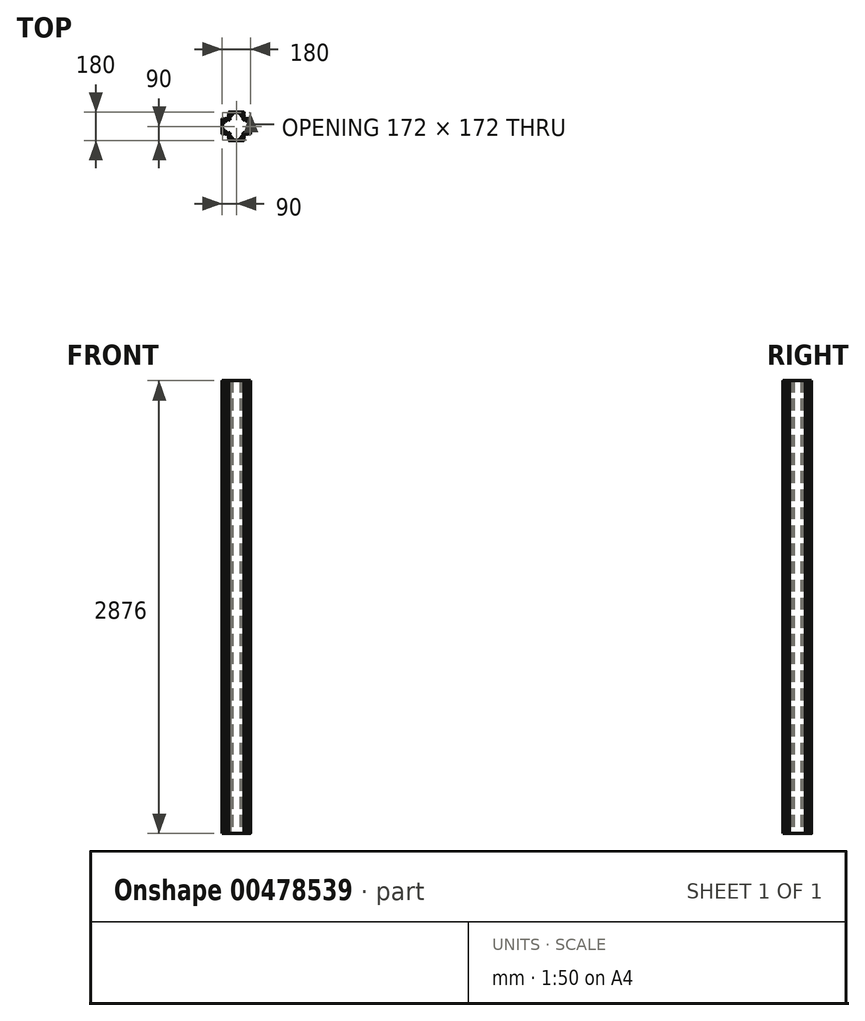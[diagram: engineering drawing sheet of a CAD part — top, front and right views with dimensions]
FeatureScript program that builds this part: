
annotation { "Feature Type Name" : "Feature", "Feature Type Description" : "" }
export const myFeature = defineFeature(function(context is Context, id is Id, definition is map)
    precondition{}
    {
        {
            var Q0;
            Q0=qCreatedBy(makeId("Top.planeOp"),FACE);
            var sketch = newSketch(context, id + "F0", { "sketchPlane" : qUnion([Q0])});
            skLineSegment(sketch, "E0", {"start": v(-58.4, 0) * mm, "end": v(68.52, 0) * mm, "construction": true});
            skLineSegment(sketch, "E1", {"start": v(0, 55.81) * mm, "end": v(0, -52.18) * mm, "construction": true});
            skLineSegment(sketch, "E2.bottom", {"start": v(-50, 90) * mm, "end": v(50, 90) * mm});
            skLineSegment(sketch, "E2.top", {"start": v(-50, -90) * mm, "end": v(50, -90) * mm});
            skLineSegment(sketch, "E2.left", {"start": v(-90, 50) * mm, "end": v(-90, -50) * mm});
            skLineSegment(sketch, "E2.right", {"start": v(90, 50) * mm, "end": v(90, -50) * mm});
            skLineSegment(sketch, "E3", {"start": v(-90, 50) * mm, "end": v(-82, 50) * mm});
            skLineSegment(sketch, "E4", {"start": v(-50, 50) * mm, "end": v(-50, 72) * mm});
            skLineSegment(sketch, "E5.MirrorCS", {"start": v(90, 50) * mm, "end": v(82, 50) * mm});
            skLineSegment(sketch, "E6.MirrorCS", {"start": v(50, 50) * mm, "end": v(50, 72) * mm});
            skLineSegment(sketch, "E7.MirrorCS", {"start": v(50, -50) * mm, "end": v(50, -72) * mm});
            skLineSegment(sketch, "E8.MirrorCS", {"start": v(90, -50) * mm, "end": v(82, -50) * mm});
            skLineSegment(sketch, "E9.MirrorCS", {"start": v(-50, -50) * mm, "end": v(-50, -72) * mm});
            skLineSegment(sketch, "E10.MirrorCS", {"start": v(-90, -50) * mm, "end": v(-82, -50) * mm});
            skLineSegment(sketch, "E11", {"start": v(-82, -50) * mm, "end": v(-82, -46) * mm});
            skLineSegment(sketch, "E12", {"start": v(-82, -46) * mm, "end": v(-86, -46) * mm});
            skLineSegment(sketch, "E13", {"start": v(-86, -46) * mm, "end": v(-86, -38) * mm});
            skLineSegment(sketch, "E14", {"start": v(-86, -38) * mm, "end": v(-68, -38) * mm});
            skLineSegment(sketch, "E15", {"start": v(-68, -38) * mm, "end": v(-68, -46) * mm});
            skLineSegment(sketch, "E16", {"start": v(-68, -46) * mm, "end": v(-72, -46) * mm});
            skLineSegment(sketch, "E17", {"start": v(-72, -46) * mm, "end": v(-72, -50) * mm});
            skLineSegment(sketch, "E18.MirrorCS", {"start": v(-68, 46) * mm, "end": v(-72, 46) * mm});
            skLineSegment(sketch, "E19.MirrorCS", {"start": v(-86, 38) * mm, "end": v(-68, 38) * mm});
            skLineSegment(sketch, "E20.MirrorCS", {"start": v(-82, 50) * mm, "end": v(-82, 46) * mm});
            skLineSegment(sketch, "E21.MirrorCS", {"start": v(-86, 46) * mm, "end": v(-86, 38) * mm});
            skLineSegment(sketch, "E22.MirrorCS", {"start": v(-82, 46) * mm, "end": v(-86, 46) * mm});
            skLineSegment(sketch, "E23.MirrorCS", {"start": v(-68, 38) * mm, "end": v(-68, 46) * mm});
            skLineSegment(sketch, "E24.MirrorCS", {"start": v(-72, 46) * mm, "end": v(-72, 50) * mm});
            skLineSegment(sketch, "E25.MirrorCS", {"start": v(68, -38) * mm, "end": v(68, -46) * mm});
            skLineSegment(sketch, "E26.MirrorCS", {"start": v(86, 38) * mm, "end": v(68, 38) * mm});
            skLineSegment(sketch, "E27.MirrorCS", {"start": v(82, 46) * mm, "end": v(86, 46) * mm});
            skLineSegment(sketch, "E28.MirrorCS", {"start": v(86, -38) * mm, "end": v(68, -38) * mm});
            skLineSegment(sketch, "E29.MirrorCS", {"start": v(68, 46) * mm, "end": v(72, 46) * mm});
            skLineSegment(sketch, "E30.MirrorCS", {"start": v(86, 46) * mm, "end": v(86, 38) * mm});
            skLineSegment(sketch, "E31.MirrorCS", {"start": v(86, -46) * mm, "end": v(86, -38) * mm});
            skLineSegment(sketch, "E32.MirrorCS", {"start": v(72, -46) * mm, "end": v(72, -50) * mm});
            skLineSegment(sketch, "E33.MirrorCS", {"start": v(82, 50) * mm, "end": v(82, 46) * mm});
            skLineSegment(sketch, "E34.MirrorCS", {"start": v(72, 46) * mm, "end": v(72, 50) * mm});
            skLineSegment(sketch, "E35.MirrorCS", {"start": v(68, 38) * mm, "end": v(68, 46) * mm});
            skLineSegment(sketch, "E36.MirrorCS", {"start": v(82, -50) * mm, "end": v(82, -46) * mm});
            skLineSegment(sketch, "E37.MirrorCS", {"start": v(68, -46) * mm, "end": v(72, -46) * mm});
            skLineSegment(sketch, "E38.MirrorCS", {"start": v(82, -46) * mm, "end": v(86, -46) * mm});
            skLineSegment(sketch, "E39", {"start": v(-50, 50) * mm, "end": v(0, 0) * mm, "construction": true});
            skLineSegment(sketch, "E40.MirrorCS", {"start": v(-38, 68) * mm, "end": v(-46, 68) * mm});
            skLineSegment(sketch, "E41.MirrorCS", {"start": v(-46, 68) * mm, "end": v(-46, 72) * mm});
            skLineSegment(sketch, "E42.MirrorCS", {"start": v(-46, 72) * mm, "end": v(-50, 72) * mm});
            skLineSegment(sketch, "E43.MirrorCS", {"start": v(-38, 86) * mm, "end": v(-38, 68) * mm});
            skLineSegment(sketch, "E44.MirrorCS", {"start": v(-46, 86) * mm, "end": v(-38, 86) * mm});
            skLineSegment(sketch, "E45.MirrorCS", {"start": v(-50, 82) * mm, "end": v(-46, 82) * mm});
            skLineSegment(sketch, "E46.MirrorCS", {"start": v(-46, 82) * mm, "end": v(-46, 86) * mm});
            skLineSegment(sketch, "E47.MirrorCS", {"start": v(46, 82) * mm, "end": v(46, 86) * mm});
            skLineSegment(sketch, "E48.MirrorCS", {"start": v(38, 86) * mm, "end": v(38, 68) * mm});
            skLineSegment(sketch, "E49.MirrorCS", {"start": v(46, 68) * mm, "end": v(46, 72) * mm});
            skLineSegment(sketch, "E50.MirrorCS", {"start": v(50, 82) * mm, "end": v(46, 82) * mm});
            skLineSegment(sketch, "E51.MirrorCS", {"start": v(46, 86) * mm, "end": v(38, 86) * mm});
            skLineSegment(sketch, "E52.MirrorCS", {"start": v(38, 68) * mm, "end": v(46, 68) * mm});
            skLineSegment(sketch, "E53.MirrorCS", {"start": v(46, 72) * mm, "end": v(50, 72) * mm});
            skLineSegment(sketch, "E54.MirrorCS", {"start": v(-46, -86) * mm, "end": v(-38, -86) * mm});
            skLineSegment(sketch, "E55.MirrorCS", {"start": v(50, -82) * mm, "end": v(46, -82) * mm});
            skLineSegment(sketch, "E56.MirrorCS", {"start": v(-38, -86) * mm, "end": v(-38, -68) * mm});
            skLineSegment(sketch, "E57.MirrorCS", {"start": v(-46, -82) * mm, "end": v(-46, -86) * mm});
            skLineSegment(sketch, "E58.MirrorCS", {"start": v(-38, -68) * mm, "end": v(-46, -68) * mm});
            skLineSegment(sketch, "E59.MirrorCS", {"start": v(38, -86) * mm, "end": v(38, -68) * mm});
            skLineSegment(sketch, "E60.MirrorCS", {"start": v(-50, -82) * mm, "end": v(-46, -82) * mm});
            skLineSegment(sketch, "E61.MirrorCS", {"start": v(-46, -72) * mm, "end": v(-50, -72) * mm});
            skLineSegment(sketch, "E62.MirrorCS", {"start": v(-46, -68) * mm, "end": v(-46, -72) * mm});
            skLineSegment(sketch, "E63.MirrorCS", {"start": v(46, -72) * mm, "end": v(50, -72) * mm});
            skLineSegment(sketch, "E64.MirrorCS", {"start": v(38, -68) * mm, "end": v(46, -68) * mm});
            skLineSegment(sketch, "E65.MirrorCS", {"start": v(46, -68) * mm, "end": v(46, -72) * mm});
            skLineSegment(sketch, "E66.MirrorCS", {"start": v(46, -82) * mm, "end": v(46, -86) * mm});
            skLineSegment(sketch, "E67.MirrorCS", {"start": v(46, -86) * mm, "end": v(38, -86) * mm});
            skLineSegment(sketch, "E68.trimOffspring", {"start": v(-72, 50) * mm, "end": v(-50, 50) * mm});
            skLineSegment(sketch, "E69.trimOffspring", {"start": v(-50, 82) * mm, "end": v(-50, 90) * mm});
            skLineSegment(sketch, "E70.trimOffspring", {"start": v(50, 82) * mm, "end": v(50, 90) * mm});
            skLineSegment(sketch, "E71.trimOffspring", {"start": v(72, 50) * mm, "end": v(50, 50) * mm});
            skLineSegment(sketch, "E72.trimOffspring", {"start": v(72, -50) * mm, "end": v(50, -50) * mm});
            skLineSegment(sketch, "E73.trimOffspring", {"start": v(50, -82) * mm, "end": v(50, -90) * mm});
            skLineSegment(sketch, "E74.trimOffspring", {"start": v(-50, -82) * mm, "end": v(-50, -90) * mm});
            skLineSegment(sketch, "E75.trimOffspring", {"start": v(-72, -50) * mm, "end": v(-50, -50) * mm});
            skSolve(sketch);
        }
        {
            var Q0;
            Q0 = qSketchRegion(id + "F0", true);
            extrude(context, id + "F1", {"entities" : qUnion([Q0]), "depth" : 2876 * mm, "offsetDistance" : 25 * mm});
        }
        {
            var Q0;
            Q0=makeQuery(id+"F1.opExtrude","CAP_FACE",FACE,{"disambiguationData":[OSD([sQuery(id+"F0.wireOp",EDGE,"E2.bottom"),sQuery(id+"F0.wireOp",EDGE,"E2.top"),sQuery(id+"F0.wireOp",EDGE,"E2.left"),sQuery(id+"F0.wireOp",EDGE,"E2.right"),sQuery(id+"F0.wireOp",EDGE,"E3"),sQuery(id+"F0.wireOp",EDGE,"E4"),sQuery(id+"F0.wireOp",EDGE,"E5.MirrorCS"),sQuery(id+"F0.wireOp",EDGE,"E6.MirrorCS"),sQuery(id+"F0.wireOp",EDGE,"E7.MirrorCS"),sQuery(id+"F0.wireOp",EDGE,"E8.MirrorCS"),sQuery(id+"F0.wireOp",EDGE,"E9.MirrorCS"),sQuery(id+"F0.wireOp",EDGE,"E10.MirrorCS")])],"isStart":false});
            var Q1;
            Q1=makeQuery(id+"F1.opExtrude","CAP_FACE",FACE,{"disambiguationData":[OSD([sQuery(id+"F0.wireOp",EDGE,"E2.bottom"),sQuery(id+"F0.wireOp",EDGE,"E2.top"),sQuery(id+"F0.wireOp",EDGE,"E2.left"),sQuery(id+"F0.wireOp",EDGE,"E2.right"),sQuery(id+"F0.wireOp",EDGE,"E3"),sQuery(id+"F0.wireOp",EDGE,"E4"),sQuery(id+"F0.wireOp",EDGE,"E5.MirrorCS"),sQuery(id+"F0.wireOp",EDGE,"E6.MirrorCS"),sQuery(id+"F0.wireOp",EDGE,"E7.MirrorCS"),sQuery(id+"F0.wireOp",EDGE,"E8.MirrorCS"),sQuery(id+"F0.wireOp",EDGE,"E9.MirrorCS"),sQuery(id+"F0.wireOp",EDGE,"E10.MirrorCS")])],"isStart":true});
            shell(context, id + "F2", {"entities" : qUnion([Q0, Q1]), "thickness" : 4 * mm});
        }
        {
            var Q0;
            Q0=makeQuery(id+"F1.opExtrude","SWEPT_EDGE",EDGE,{"disambiguationData":[OSD([sQuery(id+"F0.wireOp",EDGE,"E2.top"),sQuery(id+"F0.wireOp",EDGE,"E74.trimOffspring")])]});
            var Q1;
            Q1=makeQuery(id+"F1.opExtrude","SWEPT_EDGE",EDGE,{"disambiguationData":[OSD([sQuery(id+"F0.wireOp",EDGE,"E2.left"),sQuery(id+"F0.wireOp",EDGE,"E10.MirrorCS")])]});
            var Q2;
            Q2=makeQuery(id+"F1.opExtrude","SWEPT_EDGE",EDGE,{"disambiguationData":[OSD([sQuery(id+"F0.wireOp",EDGE,"E2.top"),sQuery(id+"F0.wireOp",EDGE,"E73.trimOffspring")])]});
            var Q3;
            Q3=makeQuery(id+"F1.opExtrude","SWEPT_EDGE",EDGE,{"disambiguationData":[OSD([sQuery(id+"F0.wireOp",EDGE,"E2.right"),sQuery(id+"F0.wireOp",EDGE,"E8.MirrorCS")])]});
            var Q4;
            Q4=makeQuery(id+"F1.opExtrude","SWEPT_EDGE",EDGE,{"disambiguationData":[OSD([sQuery(id+"F0.wireOp",EDGE,"E2.right"),sQuery(id+"F0.wireOp",EDGE,"E5.MirrorCS")])]});
            var Q5;
            Q5=makeQuery(id+"F1.opExtrude","SWEPT_EDGE",EDGE,{"disambiguationData":[OSD([sQuery(id+"F0.wireOp",EDGE,"E2.bottom"),sQuery(id+"F0.wireOp",EDGE,"E70.trimOffspring")])]});
            var Q6;
            Q6=makeQuery(id+"F1.opExtrude","SWEPT_EDGE",EDGE,{"disambiguationData":[OSD([sQuery(id+"F0.wireOp",EDGE,"E2.bottom"),sQuery(id+"F0.wireOp",EDGE,"E69.trimOffspring")])]});
            var Q7;
            Q7=makeQuery(id+"F1.opExtrude","SWEPT_EDGE",EDGE,{"disambiguationData":[OSD([sQuery(id+"F0.wireOp",EDGE,"E2.left"),sQuery(id+"F0.wireOp",EDGE,"E3")])]});
            fillet(context, id + "F3", {"entities" : qUnion([Q0, Q1, Q2, Q3, Q4, Q5, Q6, Q7]), "radius" : 3 * mm, "tangentPropagation" : true, "allowEdgeOverflow" : false});
        }
        {
            var Q0;
            Q0=makeQuery(id+"F1.opExtrude","CAP_FACE",FACE,{"disambiguationData":[OSD([sQuery(id+"F0.wireOp",EDGE,"E2.bottom"),sQuery(id+"F0.wireOp",EDGE,"E2.top"),sQuery(id+"F0.wireOp",EDGE,"E2.left"),sQuery(id+"F0.wireOp",EDGE,"E2.right"),sQuery(id+"F0.wireOp",EDGE,"E3"),sQuery(id+"F0.wireOp",EDGE,"E4"),sQuery(id+"F0.wireOp",EDGE,"E5.MirrorCS"),sQuery(id+"F0.wireOp",EDGE,"E6.MirrorCS"),sQuery(id+"F0.wireOp",EDGE,"E7.MirrorCS"),sQuery(id+"F0.wireOp",EDGE,"E8.MirrorCS"),sQuery(id+"F0.wireOp",EDGE,"E9.MirrorCS"),sQuery(id+"F0.wireOp",EDGE,"E10.MirrorCS"),sQuery(id+"F0.wireOp",EDGE,"E11"),sQuery(id+"F0.wireOp",EDGE,"E12"),sQuery(id+"F0.wireOp",EDGE,"E13"),sQuery(id+"F0.wireOp",EDGE,"E14"),sQuery(id+"F0.wireOp",EDGE,"E15"),sQuery(id+"F0.wireOp",EDGE,"E16"),sQuery(id+"F0.wireOp",EDGE,"E17"),sQuery(id+"F0.wireOp",EDGE,"E18.MirrorCS"),sQuery(id+"F0.wireOp",EDGE,"E19.MirrorCS"),sQuery(id+"F0.wireOp",EDGE,"E20.MirrorCS"),sQuery(id+"F0.wireOp",EDGE,"E21.MirrorCS"),sQuery(id+"F0.wireOp",EDGE,"E22.MirrorCS"),sQuery(id+"F0.wireOp",EDGE,"E23.MirrorCS"),sQuery(id+"F0.wireOp",EDGE,"E24.MirrorCS"),sQuery(id+"F0.wireOp",EDGE,"E25.MirrorCS"),sQuery(id+"F0.wireOp",EDGE,"E26.MirrorCS"),sQuery(id+"F0.wireOp",EDGE,"E27.MirrorCS"),sQuery(id+"F0.wireOp",EDGE,"E28.MirrorCS"),sQuery(id+"F0.wireOp",EDGE,"E29.MirrorCS"),sQuery(id+"F0.wireOp",EDGE,"E30.MirrorCS"),sQuery(id+"F0.wireOp",EDGE,"E31.MirrorCS"),sQuery(id+"F0.wireOp",EDGE,"E32.MirrorCS"),sQuery(id+"F0.wireOp",EDGE,"E33.MirrorCS"),sQuery(id+"F0.wireOp",EDGE,"E34.MirrorCS"),sQuery(id+"F0.wireOp",EDGE,"E35.MirrorCS"),sQuery(id+"F0.wireOp",EDGE,"E36.MirrorCS"),sQuery(id+"F0.wireOp",EDGE,"E37.MirrorCS"),sQuery(id+"F0.wireOp",EDGE,"E38.MirrorCS"),sQuery(id+"F0.wireOp",EDGE,"E40.MirrorCS"),sQuery(id+"F0.wireOp",EDGE,"E41.MirrorCS"),sQuery(id+"F0.wireOp",EDGE,"E42.MirrorCS"),sQuery(id+"F0.wireOp",EDGE,"E43.MirrorCS"),sQuery(id+"F0.wireOp",EDGE,"E44.MirrorCS"),sQuery(id+"F0.wireOp",EDGE,"E45.MirrorCS"),sQuery(id+"F0.wireOp",EDGE,"E46.MirrorCS"),sQuery(id+"F0.wireOp",EDGE,"E47.MirrorCS"),sQuery(id+"F0.wireOp",EDGE,"E48.MirrorCS"),sQuery(id+"F0.wireOp",EDGE,"E49.MirrorCS"),sQuery(id+"F0.wireOp",EDGE,"E50.MirrorCS"),sQuery(id+"F0.wireOp",EDGE,"E51.MirrorCS"),sQuery(id+"F0.wireOp",EDGE,"E52.MirrorCS"),sQuery(id+"F0.wireOp",EDGE,"E53.MirrorCS"),sQuery(id+"F0.wireOp",EDGE,"E54.MirrorCS"),sQuery(id+"F0.wireOp",EDGE,"E55.MirrorCS"),sQuery(id+"F0.wireOp",EDGE,"E56.MirrorCS"),sQuery(id+"F0.wireOp",EDGE,"E57.MirrorCS"),sQuery(id+"F0.wireOp",EDGE,"E58.MirrorCS"),sQuery(id+"F0.wireOp",EDGE,"E59.MirrorCS"),sQuery(id+"F0.wireOp",EDGE,"E60.MirrorCS"),sQuery(id+"F0.wireOp",EDGE,"E61.MirrorCS"),sQuery(id+"F0.wireOp",EDGE,"E62.MirrorCS"),sQuery(id+"F0.wireOp",EDGE,"E63.MirrorCS"),sQuery(id+"F0.wireOp",EDGE,"E64.MirrorCS"),sQuery(id+"F0.wireOp",EDGE,"E65.MirrorCS"),sQuery(id+"F0.wireOp",EDGE,"E66.MirrorCS"),sQuery(id+"F0.wireOp",EDGE,"E67.MirrorCS"),sQuery(id+"F0.wireOp",EDGE,"E68.trimOffspring"),sQuery(id+"F0.wireOp",EDGE,"E69.trimOffspring"),sQuery(id+"F0.wireOp",EDGE,"E70.trimOffspring"),sQuery(id+"F0.wireOp",EDGE,"E71.trimOffspring"),sQuery(id+"F0.wireOp",EDGE,"E72.trimOffspring"),sQuery(id+"F0.wireOp",EDGE,"E73.trimOffspring"),sQuery(id+"F0.wireOp",EDGE,"E74.trimOffspring"),sQuery(id+"F0.wireOp",EDGE,"E75.trimOffspring")])],"isStart":true});
            var sketch = newSketch(context, id + "F4", { "sketchPlane" : qUnion([Q0])});
            skLineSegment(sketch, "E76.bottom", {"start": v(-64, 38) * mm, "end": v(-61, 38) * mm});
            skLineSegment(sketch, "E76.top", {"start": v(-64, 34) * mm, "end": v(-61, 34) * mm});
            skLineSegment(sketch, "E76.left", {"start": v(-64, 38) * mm, "end": v(-64, 34) * mm});
            skLineSegment(sketch, "E76.right", {"start": v(-61, 38) * mm, "end": v(-61, 34) * mm});
            skLineSegment(sketch, "E77", {"start": v(-74, 34) * mm, "end": v(-74, 23) * mm});
            skLineSegment(sketch, "E78", {"start": v(-74, 23) * mm, "end": v(-78, 23) * mm});
            skLineSegment(sketch, "E79", {"start": v(-78, 23) * mm, "end": v(-78, 34) * mm});
            skLineSegment(sketch, "E80", {"start": v(-78, 34) * mm, "end": v(-74, 34) * mm});
            skLineSegment(sketch, "E81", {"start": v(0, 86) * mm, "end": v(0, 0) * mm, "construction": true});
            skLineSegment(sketch, "E82", {"start": v(0, 0) * mm, "end": v(-86, 0) * mm, "construction": true});
            skLineSegment(sketch, "E83.MirrorCS", {"start": v(64, 38) * mm, "end": v(64, 34) * mm});
            skLineSegment(sketch, "E84.MirrorCS", {"start": v(61, 38) * mm, "end": v(61, 34) * mm});
            skLineSegment(sketch, "E85.MirrorCS", {"start": v(78, 34) * mm, "end": v(74, 34) * mm});
            skLineSegment(sketch, "E86.MirrorCS", {"start": v(74, 23) * mm, "end": v(78, 23) * mm});
            skLineSegment(sketch, "E87.MirrorCS", {"start": v(64, 38) * mm, "end": v(61, 38) * mm});
            skLineSegment(sketch, "E88.MirrorCS", {"start": v(64, 34) * mm, "end": v(61, 34) * mm});
            skLineSegment(sketch, "E89.MirrorCS", {"start": v(78, 23) * mm, "end": v(78, 34) * mm});
            skLineSegment(sketch, "E90.MirrorCS", {"start": v(74, 34) * mm, "end": v(74, 23) * mm});
            skLineSegment(sketch, "E91.MirrorCS", {"start": v(0, 0) * mm, "end": v(86, 0) * mm, "construction": true});
            skLineSegment(sketch, "E92.MirrorCS", {"start": v(74, -34) * mm, "end": v(74, -23) * mm});
            skLineSegment(sketch, "E93.MirrorCS", {"start": v(74, -23) * mm, "end": v(78, -23) * mm});
            skLineSegment(sketch, "E94.MirrorCS", {"start": v(64, -38) * mm, "end": v(61, -38) * mm});
            skLineSegment(sketch, "E95.MirrorCS", {"start": v(64, -34) * mm, "end": v(61, -34) * mm});
            skLineSegment(sketch, "E96.MirrorCS", {"start": v(-64, -38) * mm, "end": v(-61, -38) * mm});
            skLineSegment(sketch, "E97.MirrorCS", {"start": v(-64, -34) * mm, "end": v(-61, -34) * mm});
            skLineSegment(sketch, "E98.MirrorCS", {"start": v(-64, -38) * mm, "end": v(-64, -34) * mm});
            skLineSegment(sketch, "E99.MirrorCS", {"start": v(-61, -38) * mm, "end": v(-61, -34) * mm});
            skLineSegment(sketch, "E100.MirrorCS", {"start": v(-74, -34) * mm, "end": v(-74, -23) * mm});
            skLineSegment(sketch, "E101.MirrorCS", {"start": v(-74, -23) * mm, "end": v(-78, -23) * mm});
            skLineSegment(sketch, "E102.MirrorCS", {"start": v(78, -34) * mm, "end": v(74, -34) * mm});
            skLineSegment(sketch, "E103.MirrorCS", {"start": v(61, -38) * mm, "end": v(61, -34) * mm});
            skLineSegment(sketch, "E104.MirrorCS", {"start": v(78, -23) * mm, "end": v(78, -34) * mm});
            skLineSegment(sketch, "E105.MirrorCS", {"start": v(-78, -34) * mm, "end": v(-74, -34) * mm});
            skLineSegment(sketch, "E106.MirrorCS", {"start": v(-78, -23) * mm, "end": v(-78, -34) * mm});
            skLineSegment(sketch, "E107.MirrorCS", {"start": v(64, -38) * mm, "end": v(64, -34) * mm});
            skLineSegment(sketch, "E108", {"start": v(-46, 46) * mm, "end": v(0, 0) * mm, "construction": true});
            skLineSegment(sketch, "E109.MirrorCS", {"start": v(-34, 78) * mm, "end": v(-34, 74) * mm});
            skLineSegment(sketch, "E110.MirrorCS", {"start": v(-23, 78) * mm, "end": v(-34, 78) * mm});
            skLineSegment(sketch, "E111.MirrorCS", {"start": v(-23, 74) * mm, "end": v(-23, 78) * mm});
            skLineSegment(sketch, "E112.MirrorCS", {"start": v(-34, 74) * mm, "end": v(-23, 74) * mm});
            skLineSegment(sketch, "E113.MirrorCS", {"start": v(-38, 61) * mm, "end": v(-34, 61) * mm});
            skLineSegment(sketch, "E114.MirrorCS", {"start": v(-38, 64) * mm, "end": v(-34, 64) * mm});
            skLineSegment(sketch, "E115.MirrorCS", {"start": v(-38, 64) * mm, "end": v(-38, 61) * mm});
            skLineSegment(sketch, "E116.MirrorCS", {"start": v(-34, 64) * mm, "end": v(-34, 61) * mm});
            skLineSegment(sketch, "E117.MirrorCS", {"start": v(34, 78) * mm, "end": v(34, 74) * mm});
            skLineSegment(sketch, "E118.MirrorCS", {"start": v(34, 64) * mm, "end": v(34, 61) * mm});
            skLineSegment(sketch, "E119.MirrorCS", {"start": v(23, 78) * mm, "end": v(34, 78) * mm});
            skLineSegment(sketch, "E120.MirrorCS", {"start": v(23, 74) * mm, "end": v(23, 78) * mm});
            skLineSegment(sketch, "E121.MirrorCS", {"start": v(34, 74) * mm, "end": v(23, 74) * mm});
            skLineSegment(sketch, "E122.MirrorCS", {"start": v(38, 61) * mm, "end": v(34, 61) * mm});
            skLineSegment(sketch, "E123.MirrorCS", {"start": v(38, 64) * mm, "end": v(38, 61) * mm});
            skLineSegment(sketch, "E124.MirrorCS", {"start": v(38, 64) * mm, "end": v(34, 64) * mm});
            skLineSegment(sketch, "E125.MirrorCS", {"start": v(-34, -78) * mm, "end": v(-34, -74) * mm});
            skLineSegment(sketch, "E126.MirrorCS", {"start": v(34, -64) * mm, "end": v(34, -61) * mm});
            skLineSegment(sketch, "E127.MirrorCS", {"start": v(-34, -64) * mm, "end": v(-34, -61) * mm});
            skLineSegment(sketch, "E128.MirrorCS", {"start": v(34, -78) * mm, "end": v(34, -74) * mm});
            skLineSegment(sketch, "E129.MirrorCS", {"start": v(-23, -78) * mm, "end": v(-34, -78) * mm});
            skLineSegment(sketch, "E130.MirrorCS", {"start": v(23, -78) * mm, "end": v(34, -78) * mm});
            skLineSegment(sketch, "E131.MirrorCS", {"start": v(23, -74) * mm, "end": v(23, -78) * mm});
            skLineSegment(sketch, "E132.MirrorCS", {"start": v(-23, -74) * mm, "end": v(-23, -78) * mm});
            skLineSegment(sketch, "E133.MirrorCS", {"start": v(38, -64) * mm, "end": v(34, -64) * mm});
            skLineSegment(sketch, "E134.MirrorCS", {"start": v(38, -64) * mm, "end": v(38, -61) * mm});
            skLineSegment(sketch, "E135.MirrorCS", {"start": v(-38, -64) * mm, "end": v(-34, -64) * mm});
            skLineSegment(sketch, "E136.MirrorCS", {"start": v(34, -74) * mm, "end": v(23, -74) * mm});
            skLineSegment(sketch, "E137.MirrorCS", {"start": v(38, -61) * mm, "end": v(34, -61) * mm});
            skLineSegment(sketch, "E138.MirrorCS", {"start": v(-38, -61) * mm, "end": v(-34, -61) * mm});
            skLineSegment(sketch, "E139.MirrorCS", {"start": v(-34, -74) * mm, "end": v(-23, -74) * mm});
            skLineSegment(sketch, "E140.MirrorCS", {"start": v(-38, -64) * mm, "end": v(-38, -61) * mm});
            skArc(sketch, "E141", {"start": v(-45.65, -43.53) * mm, "mid": v(-47.77, -47.77) * mm, "end": v(-43.53, -45.65) * mm});
            skArc(sketch, "E142.0", {"start": v(-43.69, -41.57) * mm, "mid": v(-49.54, -49.54) * mm, "end": v(-41.57, -43.69) * mm});
            skLineSegment(sketch, "E143", {"start": v(-46, -46) * mm, "end": v(-44.23, -44.23) * mm, "construction": true});
            skLineSegment(sketch, "E144", {"start": v(-45.65, -43.53) * mm, "end": v(-43.53, -45.65) * mm, "construction": true});
            skLineSegment(sketch, "E145", {"start": v(-45.65, -43.53) * mm, "end": v(-43.69, -41.57) * mm});
            skLineSegment(sketch, "E146", {"start": v(-43.53, -45.65) * mm, "end": v(-41.57, -43.69) * mm});
            skLineSegment(sketch, "E147.MirrorCS", {"start": v(46, -46) * mm, "end": v(44.23, -44.23) * mm, "construction": true});
            skLineSegment(sketch, "E148.MirrorCS", {"start": v(45.65, -43.53) * mm, "end": v(43.53, -45.65) * mm, "construction": true});
            skArc(sketch, "E149.MirrorCS", {"start": v(43.69, -41.57) * mm, "mid": v(49.54, -49.54) * mm, "end": v(41.57, -43.69) * mm});
            skArc(sketch, "E150.MirrorCS", {"start": v(45.65, -43.53) * mm, "mid": v(47.77, -47.77) * mm, "end": v(43.53, -45.65) * mm});
            skLineSegment(sketch, "E151.MirrorCS", {"start": v(43.53, -45.65) * mm, "end": v(41.57, -43.69) * mm});
            skLineSegment(sketch, "E152.MirrorCS", {"start": v(45.65, -43.53) * mm, "end": v(43.69, -41.57) * mm});
            skLineSegment(sketch, "E153.MirrorCS", {"start": v(46, 46) * mm, "end": v(44.23, 44.23) * mm, "construction": true});
            skLineSegment(sketch, "E154.MirrorCS", {"start": v(45.65, 43.53) * mm, "end": v(43.53, 45.65) * mm, "construction": true});
            skLineSegment(sketch, "E155.MirrorCS", {"start": v(43.53, 45.65) * mm, "end": v(41.57, 43.69) * mm});
            skLineSegment(sketch, "E156.MirrorCS", {"start": v(45.65, 43.53) * mm, "end": v(43.69, 41.57) * mm});
            skLineSegment(sketch, "E157.MirrorCS", {"start": v(-46, 46) * mm, "end": v(-44.23, 44.23) * mm, "construction": true});
            skLineSegment(sketch, "E158.MirrorCS", {"start": v(-45.65, 43.53) * mm, "end": v(-43.53, 45.65) * mm, "construction": true});
            skLineSegment(sketch, "E159.MirrorCS", {"start": v(-45.65, 43.53) * mm, "end": v(-43.69, 41.57) * mm});
            skLineSegment(sketch, "E160.MirrorCS", {"start": v(-43.53, 45.65) * mm, "end": v(-41.57, 43.69) * mm});
            skArc(sketch, "E161.MirrorCS", {"start": v(43.69, 41.57) * mm, "mid": v(49.54, 49.54) * mm, "end": v(41.57, 43.69) * mm});
            skArc(sketch, "E162.MirrorCS", {"start": v(45.65, 43.53) * mm, "mid": v(47.77, 47.77) * mm, "end": v(43.53, 45.65) * mm});
            skArc(sketch, "E163.MirrorCS", {"start": v(-43.69, 41.57) * mm, "mid": v(-49.54, 49.54) * mm, "end": v(-41.57, 43.69) * mm});
            skArc(sketch, "E164.MirrorCS", {"start": v(-45.65, 43.53) * mm, "mid": v(-47.77, 47.77) * mm, "end": v(-43.53, 45.65) * mm});
            skSolve(sketch);
        }
        {
            var Q0;
            Q0 = qSketchRegion(id + "F4", true);
            var Q1;
            Q1=makeQuery(id+"F1.opExtrude","CAP_FACE",FACE,{"disambiguationData":[OSD([sQuery(id+"F0.wireOp",EDGE,"E2.bottom"),sQuery(id+"F0.wireOp",EDGE,"E2.top"),sQuery(id+"F0.wireOp",EDGE,"E2.left"),sQuery(id+"F0.wireOp",EDGE,"E2.right"),sQuery(id+"F0.wireOp",EDGE,"E3"),sQuery(id+"F0.wireOp",EDGE,"E4"),sQuery(id+"F0.wireOp",EDGE,"E5.MirrorCS"),sQuery(id+"F0.wireOp",EDGE,"E6.MirrorCS"),sQuery(id+"F0.wireOp",EDGE,"E7.MirrorCS"),sQuery(id+"F0.wireOp",EDGE,"E8.MirrorCS"),sQuery(id+"F0.wireOp",EDGE,"E9.MirrorCS"),sQuery(id+"F0.wireOp",EDGE,"E10.MirrorCS"),sQuery(id+"F0.wireOp",EDGE,"E11"),sQuery(id+"F0.wireOp",EDGE,"E12"),sQuery(id+"F0.wireOp",EDGE,"E13"),sQuery(id+"F0.wireOp",EDGE,"E14"),sQuery(id+"F0.wireOp",EDGE,"E15"),sQuery(id+"F0.wireOp",EDGE,"E16"),sQuery(id+"F0.wireOp",EDGE,"E17"),sQuery(id+"F0.wireOp",EDGE,"E18.MirrorCS"),sQuery(id+"F0.wireOp",EDGE,"E19.MirrorCS"),sQuery(id+"F0.wireOp",EDGE,"E20.MirrorCS"),sQuery(id+"F0.wireOp",EDGE,"E21.MirrorCS"),sQuery(id+"F0.wireOp",EDGE,"E22.MirrorCS"),sQuery(id+"F0.wireOp",EDGE,"E23.MirrorCS"),sQuery(id+"F0.wireOp",EDGE,"E24.MirrorCS"),sQuery(id+"F0.wireOp",EDGE,"E25.MirrorCS"),sQuery(id+"F0.wireOp",EDGE,"E26.MirrorCS"),sQuery(id+"F0.wireOp",EDGE,"E27.MirrorCS"),sQuery(id+"F0.wireOp",EDGE,"E28.MirrorCS"),sQuery(id+"F0.wireOp",EDGE,"E29.MirrorCS"),sQuery(id+"F0.wireOp",EDGE,"E30.MirrorCS"),sQuery(id+"F0.wireOp",EDGE,"E31.MirrorCS"),sQuery(id+"F0.wireOp",EDGE,"E32.MirrorCS"),sQuery(id+"F0.wireOp",EDGE,"E33.MirrorCS"),sQuery(id+"F0.wireOp",EDGE,"E34.MirrorCS"),sQuery(id+"F0.wireOp",EDGE,"E35.MirrorCS"),sQuery(id+"F0.wireOp",EDGE,"E36.MirrorCS"),sQuery(id+"F0.wireOp",EDGE,"E37.MirrorCS"),sQuery(id+"F0.wireOp",EDGE,"E38.MirrorCS"),sQuery(id+"F0.wireOp",EDGE,"E40.MirrorCS"),sQuery(id+"F0.wireOp",EDGE,"E41.MirrorCS"),sQuery(id+"F0.wireOp",EDGE,"E42.MirrorCS"),sQuery(id+"F0.wireOp",EDGE,"E43.MirrorCS"),sQuery(id+"F0.wireOp",EDGE,"E44.MirrorCS"),sQuery(id+"F0.wireOp",EDGE,"E45.MirrorCS"),sQuery(id+"F0.wireOp",EDGE,"E46.MirrorCS"),sQuery(id+"F0.wireOp",EDGE,"E47.MirrorCS"),sQuery(id+"F0.wireOp",EDGE,"E48.MirrorCS"),sQuery(id+"F0.wireOp",EDGE,"E49.MirrorCS"),sQuery(id+"F0.wireOp",EDGE,"E50.MirrorCS"),sQuery(id+"F0.wireOp",EDGE,"E51.MirrorCS"),sQuery(id+"F0.wireOp",EDGE,"E52.MirrorCS"),sQuery(id+"F0.wireOp",EDGE,"E53.MirrorCS"),sQuery(id+"F0.wireOp",EDGE,"E54.MirrorCS"),sQuery(id+"F0.wireOp",EDGE,"E55.MirrorCS"),sQuery(id+"F0.wireOp",EDGE,"E56.MirrorCS"),sQuery(id+"F0.wireOp",EDGE,"E57.MirrorCS"),sQuery(id+"F0.wireOp",EDGE,"E58.MirrorCS"),sQuery(id+"F0.wireOp",EDGE,"E59.MirrorCS"),sQuery(id+"F0.wireOp",EDGE,"E60.MirrorCS"),sQuery(id+"F0.wireOp",EDGE,"E61.MirrorCS"),sQuery(id+"F0.wireOp",EDGE,"E62.MirrorCS"),sQuery(id+"F0.wireOp",EDGE,"E63.MirrorCS"),sQuery(id+"F0.wireOp",EDGE,"E64.MirrorCS"),sQuery(id+"F0.wireOp",EDGE,"E65.MirrorCS"),sQuery(id+"F0.wireOp",EDGE,"E66.MirrorCS"),sQuery(id+"F0.wireOp",EDGE,"E67.MirrorCS"),sQuery(id+"F0.wireOp",EDGE,"E68.trimOffspring"),sQuery(id+"F0.wireOp",EDGE,"E69.trimOffspring"),sQuery(id+"F0.wireOp",EDGE,"E70.trimOffspring"),sQuery(id+"F0.wireOp",EDGE,"E71.trimOffspring"),sQuery(id+"F0.wireOp",EDGE,"E72.trimOffspring"),sQuery(id+"F0.wireOp",EDGE,"E73.trimOffspring"),sQuery(id+"F0.wireOp",EDGE,"E74.trimOffspring"),sQuery(id+"F0.wireOp",EDGE,"E75.trimOffspring")])],"isStart":false});
            extrude(context, id + "F5", {"entities" : qUnion([Q0]), "operationType" : NewBodyOperationType.ADD, "endBound" : BoundingType.UP_TO_SURFACE, "oppositeDirection" : true, "endBoundEntityFace" : qUnion([Q1]), "depth" : 25 * mm});
        }
        {
            var Q0;
            {var subQ0=sQuery(id+"F0.wireOp",EDGE,"E75.trimOffspring");var subQ1=sQuery(id+"F0.wireOp",EDGE,"E74.trimOffspring");var subQ2=sQuery(id+"F0.wireOp",EDGE,"E73.trimOffspring");var subQ3=sQuery(id+"F0.wireOp",EDGE,"E72.trimOffspring");var subQ4=sQuery(id+"F0.wireOp",EDGE,"E71.trimOffspring");var subQ5=sQuery(id+"F0.wireOp",EDGE,"E70.trimOffspring");var subQ6=sQuery(id+"F0.wireOp",EDGE,"E69.trimOffspring");var subQ7=sQuery(id+"F0.wireOp",EDGE,"E68.trimOffspring");var subQ8=sQuery(id+"F0.wireOp",EDGE,"E67.MirrorCS");var subQ9=sQuery(id+"F0.wireOp",EDGE,"E66.MirrorCS");var subQ10=sQuery(id+"F0.wireOp",EDGE,"E65.MirrorCS");var subQ11=sQuery(id+"F0.wireOp",EDGE,"E64.MirrorCS");var subQ12=sQuery(id+"F0.wireOp",EDGE,"E63.MirrorCS");var subQ13=sQuery(id+"F0.wireOp",EDGE,"E62.MirrorCS");var subQ14=sQuery(id+"F0.wireOp",EDGE,"E61.MirrorCS");var subQ15=sQuery(id+"F0.wireOp",EDGE,"E60.MirrorCS");var subQ16=sQuery(id+"F0.wireOp",EDGE,"E59.MirrorCS");var subQ17=sQuery(id+"F0.wireOp",EDGE,"E58.MirrorCS");var subQ18=sQuery(id+"F0.wireOp",EDGE,"E57.MirrorCS");var subQ19=sQuery(id+"F0.wireOp",EDGE,"E56.MirrorCS");var subQ20=sQuery(id+"F0.wireOp",EDGE,"E55.MirrorCS");var subQ21=sQuery(id+"F0.wireOp",EDGE,"E54.MirrorCS");var subQ22=sQuery(id+"F0.wireOp",EDGE,"E53.MirrorCS");var subQ23=sQuery(id+"F0.wireOp",EDGE,"E52.MirrorCS");var subQ24=sQuery(id+"F0.wireOp",EDGE,"E51.MirrorCS");var subQ25=sQuery(id+"F0.wireOp",EDGE,"E50.MirrorCS");var subQ26=sQuery(id+"F0.wireOp",EDGE,"E49.MirrorCS");var subQ27=sQuery(id+"F0.wireOp",EDGE,"E48.MirrorCS");var subQ28=sQuery(id+"F0.wireOp",EDGE,"E47.MirrorCS");var subQ29=sQuery(id+"F0.wireOp",EDGE,"E46.MirrorCS");var subQ30=sQuery(id+"F0.wireOp",EDGE,"E45.MirrorCS");var subQ31=sQuery(id+"F0.wireOp",EDGE,"E44.MirrorCS");var subQ32=sQuery(id+"F0.wireOp",EDGE,"E43.MirrorCS");var subQ33=sQuery(id+"F0.wireOp",EDGE,"E42.MirrorCS");var subQ34=sQuery(id+"F0.wireOp",EDGE,"E41.MirrorCS");var subQ35=sQuery(id+"F0.wireOp",EDGE,"E40.MirrorCS");var subQ36=sQuery(id+"F0.wireOp",EDGE,"E38.MirrorCS");var subQ37=sQuery(id+"F0.wireOp",EDGE,"E37.MirrorCS");var subQ38=sQuery(id+"F0.wireOp",EDGE,"E36.MirrorCS");var subQ39=sQuery(id+"F0.wireOp",EDGE,"E35.MirrorCS");var subQ40=sQuery(id+"F0.wireOp",EDGE,"E34.MirrorCS");var subQ41=sQuery(id+"F0.wireOp",EDGE,"E33.MirrorCS");var subQ42=sQuery(id+"F0.wireOp",EDGE,"E32.MirrorCS");var subQ43=sQuery(id+"F0.wireOp",EDGE,"E31.MirrorCS");var subQ44=sQuery(id+"F0.wireOp",EDGE,"E30.MirrorCS");var subQ45=sQuery(id+"F0.wireOp",EDGE,"E29.MirrorCS");var subQ46=sQuery(id+"F0.wireOp",EDGE,"E28.MirrorCS");var subQ47=sQuery(id+"F0.wireOp",EDGE,"E27.MirrorCS");var subQ48=sQuery(id+"F0.wireOp",EDGE,"E26.MirrorCS");var subQ49=sQuery(id+"F0.wireOp",EDGE,"E25.MirrorCS");var subQ50=sQuery(id+"F0.wireOp",EDGE,"E24.MirrorCS");var subQ51=sQuery(id+"F0.wireOp",EDGE,"E23.MirrorCS");var subQ52=sQuery(id+"F0.wireOp",EDGE,"E22.MirrorCS");var subQ53=sQuery(id+"F0.wireOp",EDGE,"E21.MirrorCS");var subQ54=sQuery(id+"F0.wireOp",EDGE,"E20.MirrorCS");var subQ55=sQuery(id+"F0.wireOp",EDGE,"E19.MirrorCS");var subQ56=sQuery(id+"F0.wireOp",EDGE,"E18.MirrorCS");var subQ57=sQuery(id+"F0.wireOp",EDGE,"E17");var subQ58=sQuery(id+"F0.wireOp",EDGE,"E16");var subQ59=sQuery(id+"F0.wireOp",EDGE,"E15");var subQ60=sQuery(id+"F0.wireOp",EDGE,"E14");var subQ61=sQuery(id+"F0.wireOp",EDGE,"E13");var subQ62=sQuery(id+"F0.wireOp",EDGE,"E12");var subQ63=sQuery(id+"F0.wireOp",EDGE,"E11");var subQ64=sQuery(id+"F0.wireOp",EDGE,"E10.MirrorCS");var subQ65=sQuery(id+"F0.wireOp",EDGE,"E9.MirrorCS");var subQ66=sQuery(id+"F0.wireOp",EDGE,"E8.MirrorCS");var subQ67=sQuery(id+"F0.wireOp",EDGE,"E7.MirrorCS");var subQ68=sQuery(id+"F0.wireOp",EDGE,"E6.MirrorCS");var subQ69=sQuery(id+"F0.wireOp",EDGE,"E5.MirrorCS");var subQ70=sQuery(id+"F0.wireOp",EDGE,"E4");var subQ71=sQuery(id+"F0.wireOp",EDGE,"E3");var subQ72=sQuery(id+"F0.wireOp",EDGE,"E2.right");var subQ73=sQuery(id+"F0.wireOp",EDGE,"E2.left");var subQ74=sQuery(id+"F0.wireOp",EDGE,"E2.top");var subQ75=sQuery(id+"F0.wireOp",EDGE,"E2.bottom");Q0=makeQuery(id+"F5.boolean.opBoolean","MERGE",FACE,{"derivedFrom":[makeQuery(id+"F1.opExtrude","CAP_FACE",FACE,{"disambiguationData":[OSD([subQ75,subQ74,subQ73,subQ72,subQ71,subQ70,subQ69,subQ68,subQ67,subQ66,subQ65,subQ64,subQ63,subQ62,subQ61,subQ60,subQ59,subQ58,subQ57,subQ56,subQ55,subQ54,subQ53,subQ52,subQ51,subQ50,subQ49,subQ48,subQ47,subQ46,subQ45,subQ44,subQ43,subQ42,subQ41,subQ40,subQ39,subQ38,subQ37,subQ36,subQ35,subQ34,subQ33,subQ32,subQ31,subQ30,subQ29,subQ28,subQ27,subQ26,subQ25,subQ24,subQ23,subQ22,subQ21,subQ20,subQ19,subQ18,subQ17,subQ16,subQ15,subQ14,subQ13,subQ12,subQ11,subQ10,subQ9,subQ8,subQ7,subQ6,subQ5,subQ4,subQ3,subQ2,subQ1,subQ0])],"isStart":false}),makeQuery(id+"F5.opExtrude","CAP_FACE",FACE,{"disambiguationData":[OSD([subQ75,subQ74,subQ73,subQ72,subQ71,subQ70,subQ69,subQ68,subQ67,subQ66,subQ65,subQ64,subQ63,subQ62,subQ61,subQ60,subQ59,subQ58,subQ57,subQ56,subQ55,subQ54,subQ53,subQ52,subQ51,subQ50,subQ49,subQ48,subQ47,subQ46,subQ45,subQ44,subQ43,subQ42,subQ41,subQ40,subQ39,subQ38,subQ37,subQ36,subQ35,subQ34,subQ33,subQ32,subQ31,subQ30,subQ29,subQ28,subQ27,subQ26,subQ25,subQ24,subQ23,subQ22,subQ21,subQ20,subQ19,subQ18,subQ17,subQ16,subQ15,subQ14,subQ13,subQ12,subQ11,subQ10,subQ9,subQ8,subQ7,subQ6,subQ5,subQ4,subQ3,subQ2,subQ1,subQ0]),OD(0.0)],"isStart":false}),makeQuery(id+"F5.opExtrude","CAP_FACE",FACE,{"disambiguationData":[OSD([subQ75,subQ74,subQ73,subQ72,subQ71,subQ70,subQ69,subQ68,subQ67,subQ66,subQ65,subQ64,subQ63,subQ62,subQ61,subQ60,subQ59,subQ58,subQ57,subQ56,subQ55,subQ54,subQ53,subQ52,subQ51,subQ50,subQ49,subQ48,subQ47,subQ46,subQ45,subQ44,subQ43,subQ42,subQ41,subQ40,subQ39,subQ38,subQ37,subQ36,subQ35,subQ34,subQ33,subQ32,subQ31,subQ30,subQ29,subQ28,subQ27,subQ26,subQ25,subQ24,subQ23,subQ22,subQ21,subQ20,subQ19,subQ18,subQ17,subQ16,subQ15,subQ14,subQ13,subQ12,subQ11,subQ10,subQ9,subQ8,subQ7,subQ6,subQ5,subQ4,subQ3,subQ2,subQ1,subQ0]),OD(1.0)],"isStart":false}),makeQuery(id+"F5.opExtrude","CAP_FACE",FACE,{"disambiguationData":[OSD([subQ75,subQ74,subQ73,subQ72,subQ71,subQ70,subQ69,subQ68,subQ67,subQ66,subQ65,subQ64,subQ63,subQ62,subQ61,subQ60,subQ59,subQ58,subQ57,subQ56,subQ55,subQ54,subQ53,subQ52,subQ51,subQ50,subQ49,subQ48,subQ47,subQ46,subQ45,subQ44,subQ43,subQ42,subQ41,subQ40,subQ39,subQ38,subQ37,subQ36,subQ35,subQ34,subQ33,subQ32,subQ31,subQ30,subQ29,subQ28,subQ27,subQ26,subQ25,subQ24,subQ23,subQ22,subQ21,subQ20,subQ19,subQ18,subQ17,subQ16,subQ15,subQ14,subQ13,subQ12,subQ11,subQ10,subQ9,subQ8,subQ7,subQ6,subQ5,subQ4,subQ3,subQ2,subQ1,subQ0]),OD(2.0)],"isStart":false}),makeQuery(id+"F5.opExtrude","CAP_FACE",FACE,{"disambiguationData":[OSD([subQ75,subQ74,subQ73,subQ72,subQ71,subQ70,subQ69,subQ68,subQ67,subQ66,subQ65,subQ64,subQ63,subQ62,subQ61,subQ60,subQ59,subQ58,subQ57,subQ56,subQ55,subQ54,subQ53,subQ52,subQ51,subQ50,subQ49,subQ48,subQ47,subQ46,subQ45,subQ44,subQ43,subQ42,subQ41,subQ40,subQ39,subQ38,subQ37,subQ36,subQ35,subQ34,subQ33,subQ32,subQ31,subQ30,subQ29,subQ28,subQ27,subQ26,subQ25,subQ24,subQ23,subQ22,subQ21,subQ20,subQ19,subQ18,subQ17,subQ16,subQ15,subQ14,subQ13,subQ12,subQ11,subQ10,subQ9,subQ8,subQ7,subQ6,subQ5,subQ4,subQ3,subQ2,subQ1,subQ0]),OD(3.0)],"isStart":false}),makeQuery(id+"F5.opExtrude","CAP_FACE",FACE,{"disambiguationData":[OSD([subQ75,subQ74,subQ73,subQ72,subQ71,subQ70,subQ69,subQ68,subQ67,subQ66,subQ65,subQ64,subQ63,subQ62,subQ61,subQ60,subQ59,subQ58,subQ57,subQ56,subQ55,subQ54,subQ53,subQ52,subQ51,subQ50,subQ49,subQ48,subQ47,subQ46,subQ45,subQ44,subQ43,subQ42,subQ41,subQ40,subQ39,subQ38,subQ37,subQ36,subQ35,subQ34,subQ33,subQ32,subQ31,subQ30,subQ29,subQ28,subQ27,subQ26,subQ25,subQ24,subQ23,subQ22,subQ21,subQ20,subQ19,subQ18,subQ17,subQ16,subQ15,subQ14,subQ13,subQ12,subQ11,subQ10,subQ9,subQ8,subQ7,subQ6,subQ5,subQ4,subQ3,subQ2,subQ1,subQ0]),OD(4.0)],"isStart":false}),makeQuery(id+"F5.opExtrude","CAP_FACE",FACE,{"disambiguationData":[OSD([subQ75,subQ74,subQ73,subQ72,subQ71,subQ70,subQ69,subQ68,subQ67,subQ66,subQ65,subQ64,subQ63,subQ62,subQ61,subQ60,subQ59,subQ58,subQ57,subQ56,subQ55,subQ54,subQ53,subQ52,subQ51,subQ50,subQ49,subQ48,subQ47,subQ46,subQ45,subQ44,subQ43,subQ42,subQ41,subQ40,subQ39,subQ38,subQ37,subQ36,subQ35,subQ34,subQ33,subQ32,subQ31,subQ30,subQ29,subQ28,subQ27,subQ26,subQ25,subQ24,subQ23,subQ22,subQ21,subQ20,subQ19,subQ18,subQ17,subQ16,subQ15,subQ14,subQ13,subQ12,subQ11,subQ10,subQ9,subQ8,subQ7,subQ6,subQ5,subQ4,subQ3,subQ2,subQ1,subQ0]),OD(5.0)],"isStart":false}),makeQuery(id+"F5.opExtrude","CAP_FACE",FACE,{"disambiguationData":[OSD([subQ75,subQ74,subQ73,subQ72,subQ71,subQ70,subQ69,subQ68,subQ67,subQ66,subQ65,subQ64,subQ63,subQ62,subQ61,subQ60,subQ59,subQ58,subQ57,subQ56,subQ55,subQ54,subQ53,subQ52,subQ51,subQ50,subQ49,subQ48,subQ47,subQ46,subQ45,subQ44,subQ43,subQ42,subQ41,subQ40,subQ39,subQ38,subQ37,subQ36,subQ35,subQ34,subQ33,subQ32,subQ31,subQ30,subQ29,subQ28,subQ27,subQ26,subQ25,subQ24,subQ23,subQ22,subQ21,subQ20,subQ19,subQ18,subQ17,subQ16,subQ15,subQ14,subQ13,subQ12,subQ11,subQ10,subQ9,subQ8,subQ7,subQ6,subQ5,subQ4,subQ3,subQ2,subQ1,subQ0]),OD(6.0)],"isStart":false}),makeQuery(id+"F5.opExtrude","CAP_FACE",FACE,{"disambiguationData":[OSD([subQ75,subQ74,subQ73,subQ72,subQ71,subQ70,subQ69,subQ68,subQ67,subQ66,subQ65,subQ64,subQ63,subQ62,subQ61,subQ60,subQ59,subQ58,subQ57,subQ56,subQ55,subQ54,subQ53,subQ52,subQ51,subQ50,subQ49,subQ48,subQ47,subQ46,subQ45,subQ44,subQ43,subQ42,subQ41,subQ40,subQ39,subQ38,subQ37,subQ36,subQ35,subQ34,subQ33,subQ32,subQ31,subQ30,subQ29,subQ28,subQ27,subQ26,subQ25,subQ24,subQ23,subQ22,subQ21,subQ20,subQ19,subQ18,subQ17,subQ16,subQ15,subQ14,subQ13,subQ12,subQ11,subQ10,subQ9,subQ8,subQ7,subQ6,subQ5,subQ4,subQ3,subQ2,subQ1,subQ0]),OD(7.0)],"isStart":false}),makeQuery(id+"F5.opExtrude","CAP_FACE",FACE,{"disambiguationData":[OSD([subQ75,subQ74,subQ73,subQ72,subQ71,subQ70,subQ69,subQ68,subQ67,subQ66,subQ65,subQ64,subQ63,subQ62,subQ61,subQ60,subQ59,subQ58,subQ57,subQ56,subQ55,subQ54,subQ53,subQ52,subQ51,subQ50,subQ49,subQ48,subQ47,subQ46,subQ45,subQ44,subQ43,subQ42,subQ41,subQ40,subQ39,subQ38,subQ37,subQ36,subQ35,subQ34,subQ33,subQ32,subQ31,subQ30,subQ29,subQ28,subQ27,subQ26,subQ25,subQ24,subQ23,subQ22,subQ21,subQ20,subQ19,subQ18,subQ17,subQ16,subQ15,subQ14,subQ13,subQ12,subQ11,subQ10,subQ9,subQ8,subQ7,subQ6,subQ5,subQ4,subQ3,subQ2,subQ1,subQ0]),OD(8.0)],"isStart":false}),makeQuery(id+"F5.opExtrude","CAP_FACE",FACE,{"disambiguationData":[OSD([subQ75,subQ74,subQ73,subQ72,subQ71,subQ70,subQ69,subQ68,subQ67,subQ66,subQ65,subQ64,subQ63,subQ62,subQ61,subQ60,subQ59,subQ58,subQ57,subQ56,subQ55,subQ54,subQ53,subQ52,subQ51,subQ50,subQ49,subQ48,subQ47,subQ46,subQ45,subQ44,subQ43,subQ42,subQ41,subQ40,subQ39,subQ38,subQ37,subQ36,subQ35,subQ34,subQ33,subQ32,subQ31,subQ30,subQ29,subQ28,subQ27,subQ26,subQ25,subQ24,subQ23,subQ22,subQ21,subQ20,subQ19,subQ18,subQ17,subQ16,subQ15,subQ14,subQ13,subQ12,subQ11,subQ10,subQ9,subQ8,subQ7,subQ6,subQ5,subQ4,subQ3,subQ2,subQ1,subQ0]),OD(9.0)],"isStart":false}),makeQuery(id+"F5.opExtrude","CAP_FACE",FACE,{"disambiguationData":[OSD([subQ75,subQ74,subQ73,subQ72,subQ71,subQ70,subQ69,subQ68,subQ67,subQ66,subQ65,subQ64,subQ63,subQ62,subQ61,subQ60,subQ59,subQ58,subQ57,subQ56,subQ55,subQ54,subQ53,subQ52,subQ51,subQ50,subQ49,subQ48,subQ47,subQ46,subQ45,subQ44,subQ43,subQ42,subQ41,subQ40,subQ39,subQ38,subQ37,subQ36,subQ35,subQ34,subQ33,subQ32,subQ31,subQ30,subQ29,subQ28,subQ27,subQ26,subQ25,subQ24,subQ23,subQ22,subQ21,subQ20,subQ19,subQ18,subQ17,subQ16,subQ15,subQ14,subQ13,subQ12,subQ11,subQ10,subQ9,subQ8,subQ7,subQ6,subQ5,subQ4,subQ3,subQ2,subQ1,subQ0]),OD(10.0)],"isStart":false}),makeQuery(id+"F5.opExtrude","CAP_FACE",FACE,{"disambiguationData":[OSD([subQ75,subQ74,subQ73,subQ72,subQ71,subQ70,subQ69,subQ68,subQ67,subQ66,subQ65,subQ64,subQ63,subQ62,subQ61,subQ60,subQ59,subQ58,subQ57,subQ56,subQ55,subQ54,subQ53,subQ52,subQ51,subQ50,subQ49,subQ48,subQ47,subQ46,subQ45,subQ44,subQ43,subQ42,subQ41,subQ40,subQ39,subQ38,subQ37,subQ36,subQ35,subQ34,subQ33,subQ32,subQ31,subQ30,subQ29,subQ28,subQ27,subQ26,subQ25,subQ24,subQ23,subQ22,subQ21,subQ20,subQ19,subQ18,subQ17,subQ16,subQ15,subQ14,subQ13,subQ12,subQ11,subQ10,subQ9,subQ8,subQ7,subQ6,subQ5,subQ4,subQ3,subQ2,subQ1,subQ0]),OD(11.0)],"isStart":false}),makeQuery(id+"F5.opExtrude","CAP_FACE",FACE,{"disambiguationData":[OSD([subQ75,subQ74,subQ73,subQ72,subQ71,subQ70,subQ69,subQ68,subQ67,subQ66,subQ65,subQ64,subQ63,subQ62,subQ61,subQ60,subQ59,subQ58,subQ57,subQ56,subQ55,subQ54,subQ53,subQ52,subQ51,subQ50,subQ49,subQ48,subQ47,subQ46,subQ45,subQ44,subQ43,subQ42,subQ41,subQ40,subQ39,subQ38,subQ37,subQ36,subQ35,subQ34,subQ33,subQ32,subQ31,subQ30,subQ29,subQ28,subQ27,subQ26,subQ25,subQ24,subQ23,subQ22,subQ21,subQ20,subQ19,subQ18,subQ17,subQ16,subQ15,subQ14,subQ13,subQ12,subQ11,subQ10,subQ9,subQ8,subQ7,subQ6,subQ5,subQ4,subQ3,subQ2,subQ1,subQ0]),OD(12.0)],"isStart":false}),makeQuery(id+"F5.opExtrude","CAP_FACE",FACE,{"disambiguationData":[OSD([subQ75,subQ74,subQ73,subQ72,subQ71,subQ70,subQ69,subQ68,subQ67,subQ66,subQ65,subQ64,subQ63,subQ62,subQ61,subQ60,subQ59,subQ58,subQ57,subQ56,subQ55,subQ54,subQ53,subQ52,subQ51,subQ50,subQ49,subQ48,subQ47,subQ46,subQ45,subQ44,subQ43,subQ42,subQ41,subQ40,subQ39,subQ38,subQ37,subQ36,subQ35,subQ34,subQ33,subQ32,subQ31,subQ30,subQ29,subQ28,subQ27,subQ26,subQ25,subQ24,subQ23,subQ22,subQ21,subQ20,subQ19,subQ18,subQ17,subQ16,subQ15,subQ14,subQ13,subQ12,subQ11,subQ10,subQ9,subQ8,subQ7,subQ6,subQ5,subQ4,subQ3,subQ2,subQ1,subQ0]),OD(13.0)],"isStart":false}),makeQuery(id+"F5.opExtrude","CAP_FACE",FACE,{"disambiguationData":[OSD([subQ75,subQ74,subQ73,subQ72,subQ71,subQ70,subQ69,subQ68,subQ67,subQ66,subQ65,subQ64,subQ63,subQ62,subQ61,subQ60,subQ59,subQ58,subQ57,subQ56,subQ55,subQ54,subQ53,subQ52,subQ51,subQ50,subQ49,subQ48,subQ47,subQ46,subQ45,subQ44,subQ43,subQ42,subQ41,subQ40,subQ39,subQ38,subQ37,subQ36,subQ35,subQ34,subQ33,subQ32,subQ31,subQ30,subQ29,subQ28,subQ27,subQ26,subQ25,subQ24,subQ23,subQ22,subQ21,subQ20,subQ19,subQ18,subQ17,subQ16,subQ15,subQ14,subQ13,subQ12,subQ11,subQ10,subQ9,subQ8,subQ7,subQ6,subQ5,subQ4,subQ3,subQ2,subQ1,subQ0]),OD(14.0)],"isStart":false}),makeQuery(id+"F5.opExtrude","CAP_FACE",FACE,{"disambiguationData":[OSD([subQ75,subQ74,subQ73,subQ72,subQ71,subQ70,subQ69,subQ68,subQ67,subQ66,subQ65,subQ64,subQ63,subQ62,subQ61,subQ60,subQ59,subQ58,subQ57,subQ56,subQ55,subQ54,subQ53,subQ52,subQ51,subQ50,subQ49,subQ48,subQ47,subQ46,subQ45,subQ44,subQ43,subQ42,subQ41,subQ40,subQ39,subQ38,subQ37,subQ36,subQ35,subQ34,subQ33,subQ32,subQ31,subQ30,subQ29,subQ28,subQ27,subQ26,subQ25,subQ24,subQ23,subQ22,subQ21,subQ20,subQ19,subQ18,subQ17,subQ16,subQ15,subQ14,subQ13,subQ12,subQ11,subQ10,subQ9,subQ8,subQ7,subQ6,subQ5,subQ4,subQ3,subQ2,subQ1,subQ0]),OD(15.0)],"isStart":false}),makeQuery(id+"F5.opExtrude","CAP_FACE",FACE,{"disambiguationData":[OSD([subQ75,subQ74,subQ73,subQ72,subQ71,subQ70,subQ69,subQ68,subQ67,subQ66,subQ65,subQ64,subQ63,subQ62,subQ61,subQ60,subQ59,subQ58,subQ57,subQ56,subQ55,subQ54,subQ53,subQ52,subQ51,subQ50,subQ49,subQ48,subQ47,subQ46,subQ45,subQ44,subQ43,subQ42,subQ41,subQ40,subQ39,subQ38,subQ37,subQ36,subQ35,subQ34,subQ33,subQ32,subQ31,subQ30,subQ29,subQ28,subQ27,subQ26,subQ25,subQ24,subQ23,subQ22,subQ21,subQ20,subQ19,subQ18,subQ17,subQ16,subQ15,subQ14,subQ13,subQ12,subQ11,subQ10,subQ9,subQ8,subQ7,subQ6,subQ5,subQ4,subQ3,subQ2,subQ1,subQ0]),OD(16.0)],"isStart":false}),makeQuery(id+"F5.opExtrude","CAP_FACE",FACE,{"disambiguationData":[OSD([subQ75,subQ74,subQ73,subQ72,subQ71,subQ70,subQ69,subQ68,subQ67,subQ66,subQ65,subQ64,subQ63,subQ62,subQ61,subQ60,subQ59,subQ58,subQ57,subQ56,subQ55,subQ54,subQ53,subQ52,subQ51,subQ50,subQ49,subQ48,subQ47,subQ46,subQ45,subQ44,subQ43,subQ42,subQ41,subQ40,subQ39,subQ38,subQ37,subQ36,subQ35,subQ34,subQ33,subQ32,subQ31,subQ30,subQ29,subQ28,subQ27,subQ26,subQ25,subQ24,subQ23,subQ22,subQ21,subQ20,subQ19,subQ18,subQ17,subQ16,subQ15,subQ14,subQ13,subQ12,subQ11,subQ10,subQ9,subQ8,subQ7,subQ6,subQ5,subQ4,subQ3,subQ2,subQ1,subQ0]),OD(17.0)],"isStart":false}),makeQuery(id+"F5.opExtrude","CAP_FACE",FACE,{"disambiguationData":[OSD([subQ75,subQ74,subQ73,subQ72,subQ71,subQ70,subQ69,subQ68,subQ67,subQ66,subQ65,subQ64,subQ63,subQ62,subQ61,subQ60,subQ59,subQ58,subQ57,subQ56,subQ55,subQ54,subQ53,subQ52,subQ51,subQ50,subQ49,subQ48,subQ47,subQ46,subQ45,subQ44,subQ43,subQ42,subQ41,subQ40,subQ39,subQ38,subQ37,subQ36,subQ35,subQ34,subQ33,subQ32,subQ31,subQ30,subQ29,subQ28,subQ27,subQ26,subQ25,subQ24,subQ23,subQ22,subQ21,subQ20,subQ19,subQ18,subQ17,subQ16,subQ15,subQ14,subQ13,subQ12,subQ11,subQ10,subQ9,subQ8,subQ7,subQ6,subQ5,subQ4,subQ3,subQ2,subQ1,subQ0]),OD(18.0)],"isStart":false}),makeQuery(id+"F5.opExtrude","CAP_FACE",FACE,{"disambiguationData":[OSD([subQ75,subQ74,subQ73,subQ72,subQ71,subQ70,subQ69,subQ68,subQ67,subQ66,subQ65,subQ64,subQ63,subQ62,subQ61,subQ60,subQ59,subQ58,subQ57,subQ56,subQ55,subQ54,subQ53,subQ52,subQ51,subQ50,subQ49,subQ48,subQ47,subQ46,subQ45,subQ44,subQ43,subQ42,subQ41,subQ40,subQ39,subQ38,subQ37,subQ36,subQ35,subQ34,subQ33,subQ32,subQ31,subQ30,subQ29,subQ28,subQ27,subQ26,subQ25,subQ24,subQ23,subQ22,subQ21,subQ20,subQ19,subQ18,subQ17,subQ16,subQ15,subQ14,subQ13,subQ12,subQ11,subQ10,subQ9,subQ8,subQ7,subQ6,subQ5,subQ4,subQ3,subQ2,subQ1,subQ0]),OD(19.0)],"isStart":false})]});}
            var sketch = newSketch(context, id + "F6", { "sketchPlane" : qUnion([Q0])});
            skArc(sketch, "E165.0", {"start": v(-45.65, 43.53) * mm, "mid": v(-47.64, 44.11) * mm, "end": v(-48.5, 46) * mm, "construction": true});
            skCircle(sketch, "E166", {"center": v(-46, 46) * mm, "radius": 2.5 * mm});
            skCircle(sketch, "E167", {"center": v(46, 46) * mm, "radius": 2.5 * mm});
            skCircle(sketch, "E168", {"center": v(-46, -46) * mm, "radius": 2.5 * mm});
            skCircle(sketch, "E169", {"center": v(46, -46) * mm, "radius": 2.5 * mm});
            skSolve(sketch);
        }
        {
            var Q0;
            Q0 = qSketchRegion(id + "F6", true);
            extrude(context, id + "F7", {"entities" : qUnion([Q0]), "operationType" : NewBodyOperationType.REMOVE, "endBound" : BoundingType.THROUGH_ALL, "oppositeDirection" : true, "depth" : 25 * mm, "offsetDistance" : 25 * mm});
        }
        {
            var Q0;
            Q0=makeQuery(id+"F1.opExtrude","SWEPT_EDGE",EDGE,{"disambiguationData":[OSD([sQuery(id+"F0.wireOp",EDGE,"E6.MirrorCS"),sQuery(id+"F0.wireOp",EDGE,"E71.trimOffspring")])]});
            var Q1;
            Q1=makeQuery(id+"F1.opExtrude","SWEPT_EDGE",EDGE,{"disambiguationData":[OSD([sQuery(id+"F0.wireOp",EDGE,"E7.MirrorCS"),sQuery(id+"F0.wireOp",EDGE,"E72.trimOffspring")])]});
            var Q2;
            Q2=makeQuery(id+"F1.opExtrude","SWEPT_EDGE",EDGE,{"disambiguationData":[OSD([sQuery(id+"F0.wireOp",EDGE,"E9.MirrorCS"),sQuery(id+"F0.wireOp",EDGE,"E75.trimOffspring")])]});
            var Q3;
            Q3=makeQuery(id+"F1.opExtrude","SWEPT_EDGE",EDGE,{"disambiguationData":[OSD([sQuery(id+"F0.wireOp",EDGE,"E4"),sQuery(id+"F0.wireOp",EDGE,"E68.trimOffspring")])]});
            fillet(context, id + "F8", {"entities" : qUnion([Q0, Q1, Q2, Q3]), "radius" : 3 * mm, "tangentPropagation" : true, "allowEdgeOverflow" : false});
        }
        {
            var Q0;
            Q0=makeQuery(id+"F1.opExtrude","SWEPT_EDGE",EDGE,{"disambiguationData":[OSD([sQuery(id+"F0.wireOp",EDGE,"E13"),sQuery(id+"F0.wireOp",EDGE,"E14")])]});
            var Q1;
            Q1=makeQuery(id+"F1.opExtrude","SWEPT_EDGE",EDGE,{"disambiguationData":[OSD([sQuery(id+"F0.wireOp",EDGE,"E12"),sQuery(id+"F0.wireOp",EDGE,"E13")])]});
            var Q2;
            Q2=makeQuery(id+"F1.opExtrude","SWEPT_EDGE",EDGE,{"disambiguationData":[OSD([sQuery(id+"F0.wireOp",EDGE,"E14"),sQuery(id+"F0.wireOp",EDGE,"E15")])]});
            var Q3;
            Q3=makeQuery(id+"F1.opExtrude","SWEPT_EDGE",EDGE,{"disambiguationData":[OSD([sQuery(id+"F0.wireOp",EDGE,"E15"),sQuery(id+"F0.wireOp",EDGE,"E16")])]});
            var Q4;
            Q4=makeQuery(id+"F1.opExtrude","SWEPT_EDGE",EDGE,{"disambiguationData":[OSD([sQuery(id+"F0.wireOp",EDGE,"E58.MirrorCS"),sQuery(id+"F0.wireOp",EDGE,"E62.MirrorCS")])]});
            var Q5;
            Q5=makeQuery(id+"F1.opExtrude","SWEPT_EDGE",EDGE,{"disambiguationData":[OSD([sQuery(id+"F0.wireOp",EDGE,"E56.MirrorCS"),sQuery(id+"F0.wireOp",EDGE,"E58.MirrorCS")])]});
            var Q6;
            Q6=makeQuery(id+"F1.opExtrude","SWEPT_EDGE",EDGE,{"disambiguationData":[OSD([sQuery(id+"F0.wireOp",EDGE,"E54.MirrorCS"),sQuery(id+"F0.wireOp",EDGE,"E56.MirrorCS")])]});
            var Q7;
            Q7=makeQuery(id+"F1.opExtrude","SWEPT_EDGE",EDGE,{"disambiguationData":[OSD([sQuery(id+"F0.wireOp",EDGE,"E54.MirrorCS"),sQuery(id+"F0.wireOp",EDGE,"E57.MirrorCS")])]});
            var Q8;
            Q8=makeQuery(id+"F1.opExtrude","SWEPT_EDGE",EDGE,{"disambiguationData":[OSD([sQuery(id+"F0.wireOp",EDGE,"E59.MirrorCS"),sQuery(id+"F0.wireOp",EDGE,"E67.MirrorCS")])]});
            var Q9;
            Q9=makeQuery(id+"F1.opExtrude","SWEPT_EDGE",EDGE,{"disambiguationData":[OSD([sQuery(id+"F0.wireOp",EDGE,"E66.MirrorCS"),sQuery(id+"F0.wireOp",EDGE,"E67.MirrorCS")])]});
            var Q10;
            Q10=makeQuery(id+"F1.opExtrude","SWEPT_EDGE",EDGE,{"disambiguationData":[OSD([sQuery(id+"F0.wireOp",EDGE,"E59.MirrorCS"),sQuery(id+"F0.wireOp",EDGE,"E64.MirrorCS")])]});
            var Q11;
            Q11=makeQuery(id+"F1.opExtrude","SWEPT_EDGE",EDGE,{"disambiguationData":[OSD([sQuery(id+"F0.wireOp",EDGE,"E64.MirrorCS"),sQuery(id+"F0.wireOp",EDGE,"E65.MirrorCS")])]});
            var Q12;
            Q12=makeQuery(id+"F1.opExtrude","SWEPT_EDGE",EDGE,{"disambiguationData":[OSD([sQuery(id+"F0.wireOp",EDGE,"E25.MirrorCS"),sQuery(id+"F0.wireOp",EDGE,"E28.MirrorCS")])]});
            var Q13;
            Q13=makeQuery(id+"F1.opExtrude","SWEPT_EDGE",EDGE,{"disambiguationData":[OSD([sQuery(id+"F0.wireOp",EDGE,"E25.MirrorCS"),sQuery(id+"F0.wireOp",EDGE,"E37.MirrorCS")])]});
            var Q14;
            Q14=makeQuery(id+"F1.opExtrude","SWEPT_EDGE",EDGE,{"disambiguationData":[OSD([sQuery(id+"F0.wireOp",EDGE,"E28.MirrorCS"),sQuery(id+"F0.wireOp",EDGE,"E31.MirrorCS")])]});
            var Q15;
            Q15=makeQuery(id+"F1.opExtrude","SWEPT_EDGE",EDGE,{"disambiguationData":[OSD([sQuery(id+"F0.wireOp",EDGE,"E31.MirrorCS"),sQuery(id+"F0.wireOp",EDGE,"E38.MirrorCS")])]});
            var Q16;
            Q16=makeQuery(id+"F1.opExtrude","SWEPT_EDGE",EDGE,{"disambiguationData":[OSD([sQuery(id+"F0.wireOp",EDGE,"E27.MirrorCS"),sQuery(id+"F0.wireOp",EDGE,"E30.MirrorCS")])]});
            var Q17;
            Q17=makeQuery(id+"F1.opExtrude","SWEPT_EDGE",EDGE,{"disambiguationData":[OSD([sQuery(id+"F0.wireOp",EDGE,"E26.MirrorCS"),sQuery(id+"F0.wireOp",EDGE,"E30.MirrorCS")])]});
            var Q18;
            Q18=makeQuery(id+"F1.opExtrude","SWEPT_EDGE",EDGE,{"disambiguationData":[OSD([sQuery(id+"F0.wireOp",EDGE,"E26.MirrorCS"),sQuery(id+"F0.wireOp",EDGE,"E35.MirrorCS")])]});
            var Q19;
            Q19=makeQuery(id+"F1.opExtrude","SWEPT_EDGE",EDGE,{"disambiguationData":[OSD([sQuery(id+"F0.wireOp",EDGE,"E29.MirrorCS"),sQuery(id+"F0.wireOp",EDGE,"E35.MirrorCS")])]});
            var Q20;
            Q20=makeQuery(id+"F1.opExtrude","SWEPT_EDGE",EDGE,{"disambiguationData":[OSD([sQuery(id+"F0.wireOp",EDGE,"E48.MirrorCS"),sQuery(id+"F0.wireOp",EDGE,"E51.MirrorCS")])]});
            var Q21;
            Q21=makeQuery(id+"F1.opExtrude","SWEPT_EDGE",EDGE,{"disambiguationData":[OSD([sQuery(id+"F0.wireOp",EDGE,"E47.MirrorCS"),sQuery(id+"F0.wireOp",EDGE,"E51.MirrorCS")])]});
            var Q22;
            Q22=makeQuery(id+"F1.opExtrude","SWEPT_EDGE",EDGE,{"disambiguationData":[OSD([sQuery(id+"F0.wireOp",EDGE,"E48.MirrorCS"),sQuery(id+"F0.wireOp",EDGE,"E52.MirrorCS")])]});
            var Q23;
            Q23=makeQuery(id+"F1.opExtrude","SWEPT_EDGE",EDGE,{"disambiguationData":[OSD([sQuery(id+"F0.wireOp",EDGE,"E49.MirrorCS"),sQuery(id+"F0.wireOp",EDGE,"E52.MirrorCS")])]});
            var Q24;
            Q24=makeQuery(id+"F1.opExtrude","SWEPT_EDGE",EDGE,{"disambiguationData":[OSD([sQuery(id+"F0.wireOp",EDGE,"E43.MirrorCS"),sQuery(id+"F0.wireOp",EDGE,"E44.MirrorCS")])]});
            var Q25;
            Q25=makeQuery(id+"F1.opExtrude","SWEPT_EDGE",EDGE,{"disambiguationData":[OSD([sQuery(id+"F0.wireOp",EDGE,"E44.MirrorCS"),sQuery(id+"F0.wireOp",EDGE,"E46.MirrorCS")])]});
            var Q26;
            Q26=makeQuery(id+"F1.opExtrude","SWEPT_EDGE",EDGE,{"disambiguationData":[OSD([sQuery(id+"F0.wireOp",EDGE,"E40.MirrorCS"),sQuery(id+"F0.wireOp",EDGE,"E41.MirrorCS")])]});
            var Q27;
            Q27=makeQuery(id+"F1.opExtrude","SWEPT_EDGE",EDGE,{"disambiguationData":[OSD([sQuery(id+"F0.wireOp",EDGE,"E40.MirrorCS"),sQuery(id+"F0.wireOp",EDGE,"E43.MirrorCS")])]});
            var Q28;
            Q28=makeQuery(id+"F1.opExtrude","SWEPT_EDGE",EDGE,{"disambiguationData":[OSD([sQuery(id+"F0.wireOp",EDGE,"E19.MirrorCS"),sQuery(id+"F0.wireOp",EDGE,"E23.MirrorCS")])]});
            var Q29;
            Q29=makeQuery(id+"F1.opExtrude","SWEPT_EDGE",EDGE,{"disambiguationData":[OSD([sQuery(id+"F0.wireOp",EDGE,"E19.MirrorCS"),sQuery(id+"F0.wireOp",EDGE,"E21.MirrorCS")])]});
            var Q30;
            Q30=makeQuery(id+"F1.opExtrude","SWEPT_EDGE",EDGE,{"disambiguationData":[OSD([sQuery(id+"F0.wireOp",EDGE,"E21.MirrorCS"),sQuery(id+"F0.wireOp",EDGE,"E22.MirrorCS")])]});
            var Q31;
            Q31=makeQuery(id+"F1.opExtrude","SWEPT_EDGE",EDGE,{"disambiguationData":[OSD([sQuery(id+"F0.wireOp",EDGE,"E18.MirrorCS"),sQuery(id+"F0.wireOp",EDGE,"E23.MirrorCS")])]});
            fillet(context, id + "F9", {"entities" : qUnion([Q0, Q1, Q2, Q3, Q4, Q5, Q6, Q7, Q8, Q9, Q10, Q11, Q12, Q13, Q14, Q15, Q16, Q17, Q18, Q19, Q20, Q21, Q22, Q23, Q24, Q25, Q26, Q27, Q28, Q29, Q30, Q31]), "radius" : 1 * mm, "tangentPropagation" : true, "allowEdgeOverflow" : false});
        }
        {
            var Q0;
            Q0=makeQuery(id+"F5.boolean.opBoolean","INTERSECT",EDGE,{"derivedFrom":[makeQuery(id+"F2.opShell","OFFSET_FACE",FACE,{"disambiguationData":[OSD([sQuery(id+"F0.wireOp",EDGE,"E9.MirrorCS")])]}),makeQuery(id+"F5.opExtrude","SWEPT_FACE",FACE,{"disambiguationData":[OSD([sQuery(id+"F4.wireOp",EDGE,"E163.MirrorCS")])]})]});
            var Q1;
            Q1=makeQuery(id+"F5.boolean.opBoolean","INTERSECT",EDGE,{"derivedFrom":[makeQuery(id+"F2.opShell","OFFSET_FACE",FACE,{"disambiguationData":[OSD([sQuery(id+"F0.wireOp",EDGE,"E75.trimOffspring")])]}),makeQuery(id+"F5.opExtrude","SWEPT_FACE",FACE,{"disambiguationData":[OSD([sQuery(id+"F4.wireOp",EDGE,"E163.MirrorCS")])]})]});
            var Q2;
            Q2=makeQuery(id+"F5.boolean.opBoolean","INTERSECT",EDGE,{"derivedFrom":[makeQuery(id+"F2.opShell","OFFSET_FACE",FACE,{"disambiguationData":[OSD([sQuery(id+"F0.wireOp",EDGE,"E4")])]}),makeQuery(id+"F5.opExtrude","SWEPT_FACE",FACE,{"disambiguationData":[OSD([sQuery(id+"F4.wireOp",EDGE,"E142.0")])]})]});
            var Q3;
            Q3=makeQuery(id+"F5.boolean.opBoolean","INTERSECT",EDGE,{"derivedFrom":[makeQuery(id+"F2.opShell","OFFSET_FACE",FACE,{"disambiguationData":[OSD([sQuery(id+"F0.wireOp",EDGE,"E68.trimOffspring")])]}),makeQuery(id+"F5.opExtrude","SWEPT_FACE",FACE,{"disambiguationData":[OSD([sQuery(id+"F4.wireOp",EDGE,"E142.0")])]})]});
            var Q4;
            Q4=makeQuery(id+"F5.boolean.opBoolean","INTERSECT",EDGE,{"derivedFrom":[makeQuery(id+"F2.opShell","OFFSET_FACE",FACE,{"disambiguationData":[OSD([sQuery(id+"F0.wireOp",EDGE,"E71.trimOffspring")])]}),makeQuery(id+"F5.opExtrude","SWEPT_FACE",FACE,{"disambiguationData":[OSD([sQuery(id+"F4.wireOp",EDGE,"E149.MirrorCS")])]})]});
            var Q5;
            Q5=makeQuery(id+"F5.boolean.opBoolean","INTERSECT",EDGE,{"derivedFrom":[makeQuery(id+"F2.opShell","OFFSET_FACE",FACE,{"disambiguationData":[OSD([sQuery(id+"F0.wireOp",EDGE,"E6.MirrorCS")])]}),makeQuery(id+"F5.opExtrude","SWEPT_FACE",FACE,{"disambiguationData":[OSD([sQuery(id+"F4.wireOp",EDGE,"E149.MirrorCS")])]})]});
            var Q6;
            Q6=makeQuery(id+"F5.boolean.opBoolean","INTERSECT",EDGE,{"derivedFrom":[makeQuery(id+"F2.opShell","OFFSET_FACE",FACE,{"disambiguationData":[OSD([sQuery(id+"F0.wireOp",EDGE,"E7.MirrorCS")])]}),makeQuery(id+"F5.opExtrude","SWEPT_FACE",FACE,{"disambiguationData":[OSD([sQuery(id+"F4.wireOp",EDGE,"E161.MirrorCS")])]})]});
            var Q7;
            Q7=makeQuery(id+"F5.boolean.opBoolean","INTERSECT",EDGE,{"derivedFrom":[makeQuery(id+"F2.opShell","OFFSET_FACE",FACE,{"disambiguationData":[OSD([sQuery(id+"F0.wireOp",EDGE,"E72.trimOffspring")])]}),makeQuery(id+"F5.opExtrude","SWEPT_FACE",FACE,{"disambiguationData":[OSD([sQuery(id+"F4.wireOp",EDGE,"E161.MirrorCS")])]})]});
            fillet(context, id + "F10", {"entities" : qUnion([Q0, Q1, Q2, Q3, Q4, Q5, Q6, Q7]), "radius" : 2 * mm, "tangentPropagation" : true, "allowEdgeOverflow" : false});
        }
        {
            var Q0;
            Q0=makeQuery(id+"F5.opExtrude","SWEPT_EDGE",EDGE,{"disambiguationData":[OSD([sQuery(id+"F0.wireOp",EDGE,"E19.MirrorCS"),sQuery(id+"F4.wireOp",EDGE,"E105.MirrorCS"),sQuery(id+"F4.wireOp",EDGE,"E106.MirrorCS")])]});
            var Q1;
            Q1=makeQuery(id+"F5.opExtrude","SWEPT_EDGE",EDGE,{"disambiguationData":[OSD([sQuery(id+"F0.wireOp",EDGE,"E19.MirrorCS"),sQuery(id+"F4.wireOp",EDGE,"E100.MirrorCS"),sQuery(id+"F4.wireOp",EDGE,"E105.MirrorCS")])]});
            var Q2;
            Q2=makeQuery(id+"F5.opExtrude","SWEPT_EDGE",EDGE,{"disambiguationData":[OSD([sQuery(id+"F4.wireOp",EDGE,"E100.MirrorCS"),sQuery(id+"F4.wireOp",EDGE,"E101.MirrorCS")])]});
            var Q3;
            Q3=makeQuery(id+"F5.opExtrude","SWEPT_EDGE",EDGE,{"disambiguationData":[OSD([sQuery(id+"F4.wireOp",EDGE,"E101.MirrorCS"),sQuery(id+"F4.wireOp",EDGE,"E106.MirrorCS")])]});
            var Q4;
            Q4=makeQuery(id+"F5.opExtrude","SWEPT_EDGE",EDGE,{"disambiguationData":[OSD([sQuery(id+"F4.wireOp",EDGE,"E77"),sQuery(id+"F4.wireOp",EDGE,"E78")])]});
            var Q5;
            Q5=makeQuery(id+"F5.opExtrude","SWEPT_EDGE",EDGE,{"disambiguationData":[OSD([sQuery(id+"F0.wireOp",EDGE,"E14"),sQuery(id+"F4.wireOp",EDGE,"E77"),sQuery(id+"F4.wireOp",EDGE,"E80")])]});
            var Q6;
            Q6=makeQuery(id+"F5.opExtrude","SWEPT_EDGE",EDGE,{"disambiguationData":[OSD([sQuery(id+"F4.wireOp",EDGE,"E78"),sQuery(id+"F4.wireOp",EDGE,"E79")])]});
            var Q7;
            Q7=makeQuery(id+"F5.opExtrude","SWEPT_EDGE",EDGE,{"disambiguationData":[OSD([sQuery(id+"F0.wireOp",EDGE,"E14"),sQuery(id+"F4.wireOp",EDGE,"E79"),sQuery(id+"F4.wireOp",EDGE,"E80")])]});
            var Q8;
            Q8=makeQuery(id+"F5.opExtrude","SWEPT_EDGE",EDGE,{"disambiguationData":[OSD([sQuery(id+"F4.wireOp",EDGE,"E111.MirrorCS"),sQuery(id+"F4.wireOp",EDGE,"E112.MirrorCS")])]});
            var Q9;
            Q9=makeQuery(id+"F5.opExtrude","SWEPT_EDGE",EDGE,{"disambiguationData":[OSD([sQuery(id+"F4.wireOp",EDGE,"E110.MirrorCS"),sQuery(id+"F4.wireOp",EDGE,"E111.MirrorCS")])]});
            var Q10;
            Q10=makeQuery(id+"F5.opExtrude","SWEPT_EDGE",EDGE,{"disambiguationData":[OSD([sQuery(id+"F0.wireOp",EDGE,"E56.MirrorCS"),sQuery(id+"F4.wireOp",EDGE,"E109.MirrorCS"),sQuery(id+"F4.wireOp",EDGE,"E112.MirrorCS")])]});
            var Q11;
            Q11=makeQuery(id+"F5.opExtrude","SWEPT_EDGE",EDGE,{"disambiguationData":[OSD([sQuery(id+"F0.wireOp",EDGE,"E56.MirrorCS"),sQuery(id+"F4.wireOp",EDGE,"E109.MirrorCS"),sQuery(id+"F4.wireOp",EDGE,"E110.MirrorCS")])]});
            var Q12;
            Q12=makeQuery(id+"F5.opExtrude","SWEPT_EDGE",EDGE,{"disambiguationData":[OSD([sQuery(id+"F4.wireOp",EDGE,"E132.MirrorCS"),sQuery(id+"F4.wireOp",EDGE,"E139.MirrorCS")])]});
            var Q13;
            Q13=makeQuery(id+"F5.opExtrude","SWEPT_EDGE",EDGE,{"disambiguationData":[OSD([sQuery(id+"F4.wireOp",EDGE,"E129.MirrorCS"),sQuery(id+"F4.wireOp",EDGE,"E132.MirrorCS")])]});
            var Q14;
            Q14=makeQuery(id+"F5.opExtrude","SWEPT_EDGE",EDGE,{"disambiguationData":[OSD([sQuery(id+"F0.wireOp",EDGE,"E43.MirrorCS"),sQuery(id+"F4.wireOp",EDGE,"E125.MirrorCS"),sQuery(id+"F4.wireOp",EDGE,"E129.MirrorCS")])]});
            var Q15;
            Q15=makeQuery(id+"F5.opExtrude","SWEPT_EDGE",EDGE,{"disambiguationData":[OSD([sQuery(id+"F0.wireOp",EDGE,"E43.MirrorCS"),sQuery(id+"F4.wireOp",EDGE,"E125.MirrorCS"),sQuery(id+"F4.wireOp",EDGE,"E139.MirrorCS")])]});
            var Q16;
            Q16=makeQuery(id+"F5.opExtrude","SWEPT_EDGE",EDGE,{"disambiguationData":[OSD([sQuery(id+"F4.wireOp",EDGE,"E131.MirrorCS"),sQuery(id+"F4.wireOp",EDGE,"E136.MirrorCS")])]});
            var Q17;
            Q17=makeQuery(id+"F5.opExtrude","SWEPT_EDGE",EDGE,{"disambiguationData":[OSD([sQuery(id+"F4.wireOp",EDGE,"E130.MirrorCS"),sQuery(id+"F4.wireOp",EDGE,"E131.MirrorCS")])]});
            var Q18;
            Q18=makeQuery(id+"F5.opExtrude","SWEPT_EDGE",EDGE,{"disambiguationData":[OSD([sQuery(id+"F0.wireOp",EDGE,"E48.MirrorCS"),sQuery(id+"F4.wireOp",EDGE,"E128.MirrorCS"),sQuery(id+"F4.wireOp",EDGE,"E130.MirrorCS")])]});
            var Q19;
            Q19=makeQuery(id+"F5.opExtrude","SWEPT_EDGE",EDGE,{"disambiguationData":[OSD([sQuery(id+"F0.wireOp",EDGE,"E48.MirrorCS"),sQuery(id+"F4.wireOp",EDGE,"E128.MirrorCS"),sQuery(id+"F4.wireOp",EDGE,"E136.MirrorCS")])]});
            var Q20;
            Q20=makeQuery(id+"F5.opExtrude","SWEPT_EDGE",EDGE,{"disambiguationData":[OSD([sQuery(id+"F4.wireOp",EDGE,"E92.MirrorCS"),sQuery(id+"F4.wireOp",EDGE,"E93.MirrorCS")])]});
            var Q21;
            Q21=makeQuery(id+"F5.opExtrude","SWEPT_EDGE",EDGE,{"disambiguationData":[OSD([sQuery(id+"F4.wireOp",EDGE,"E86.MirrorCS"),sQuery(id+"F4.wireOp",EDGE,"E90.MirrorCS")])]});
            var Q22;
            Q22=makeQuery(id+"F5.opExtrude","SWEPT_EDGE",EDGE,{"disambiguationData":[OSD([sQuery(id+"F4.wireOp",EDGE,"E93.MirrorCS"),sQuery(id+"F4.wireOp",EDGE,"E104.MirrorCS")])]});
            var Q23;
            Q23=makeQuery(id+"F5.opExtrude","SWEPT_EDGE",EDGE,{"disambiguationData":[OSD([sQuery(id+"F0.wireOp",EDGE,"E26.MirrorCS"),sQuery(id+"F4.wireOp",EDGE,"E102.MirrorCS"),sQuery(id+"F4.wireOp",EDGE,"E104.MirrorCS")])]});
            var Q24;
            Q24=makeQuery(id+"F5.opExtrude","SWEPT_EDGE",EDGE,{"disambiguationData":[OSD([sQuery(id+"F4.wireOp",EDGE,"E86.MirrorCS"),sQuery(id+"F4.wireOp",EDGE,"E89.MirrorCS")])]});
            var Q25;
            Q25=makeQuery(id+"F5.opExtrude","SWEPT_EDGE",EDGE,{"disambiguationData":[OSD([sQuery(id+"F0.wireOp",EDGE,"E26.MirrorCS"),sQuery(id+"F4.wireOp",EDGE,"E92.MirrorCS"),sQuery(id+"F4.wireOp",EDGE,"E102.MirrorCS")])]});
            var Q26;
            Q26=makeQuery(id+"F5.opExtrude","SWEPT_EDGE",EDGE,{"disambiguationData":[OSD([sQuery(id+"F0.wireOp",EDGE,"E28.MirrorCS"),sQuery(id+"F4.wireOp",EDGE,"E85.MirrorCS"),sQuery(id+"F4.wireOp",EDGE,"E90.MirrorCS")])]});
            var Q27;
            Q27=makeQuery(id+"F5.opExtrude","SWEPT_EDGE",EDGE,{"disambiguationData":[OSD([sQuery(id+"F0.wireOp",EDGE,"E28.MirrorCS"),sQuery(id+"F4.wireOp",EDGE,"E85.MirrorCS"),sQuery(id+"F4.wireOp",EDGE,"E89.MirrorCS")])]});
            var Q28;
            Q28=makeQuery(id+"F5.opExtrude","SWEPT_EDGE",EDGE,{"disambiguationData":[OSD([sQuery(id+"F4.wireOp",EDGE,"E120.MirrorCS"),sQuery(id+"F4.wireOp",EDGE,"E121.MirrorCS")])]});
            var Q29;
            Q29=makeQuery(id+"F5.opExtrude","SWEPT_EDGE",EDGE,{"disambiguationData":[OSD([sQuery(id+"F4.wireOp",EDGE,"E119.MirrorCS"),sQuery(id+"F4.wireOp",EDGE,"E120.MirrorCS")])]});
            var Q30;
            Q30=makeQuery(id+"F5.opExtrude","SWEPT_EDGE",EDGE,{"disambiguationData":[OSD([sQuery(id+"F0.wireOp",EDGE,"E59.MirrorCS"),sQuery(id+"F4.wireOp",EDGE,"E117.MirrorCS"),sQuery(id+"F4.wireOp",EDGE,"E121.MirrorCS")])]});
            var Q31;
            Q31=makeQuery(id+"F5.opExtrude","SWEPT_EDGE",EDGE,{"disambiguationData":[OSD([sQuery(id+"F0.wireOp",EDGE,"E59.MirrorCS"),sQuery(id+"F4.wireOp",EDGE,"E117.MirrorCS"),sQuery(id+"F4.wireOp",EDGE,"E119.MirrorCS")])]});
            var Q32;
            Q32=makeQuery(id+"F2.opShell","TWEAK_EDGE",EDGE,{"derivedFrom":[makeQuery(id+"F1.opExtrude","SWEPT_FACE",FACE,{"disambiguationData":[OSD([sQuery(id+"F0.wireOp",EDGE,"E2.bottom")])]}),makeQuery(id+"F1.opExtrude","SWEPT_FACE",FACE,{"disambiguationData":[OSD([sQuery(id+"F0.wireOp",EDGE,"E48.MirrorCS")])]})]});
            var Q33;
            Q33=makeQuery(id+"F2.opShell","TWEAK_EDGE",EDGE,{"derivedFrom":[makeQuery(id+"F1.opExtrude","SWEPT_FACE",FACE,{"disambiguationData":[OSD([sQuery(id+"F0.wireOp",EDGE,"E2.bottom")])]}),makeQuery(id+"F1.opExtrude","SWEPT_FACE",FACE,{"disambiguationData":[OSD([sQuery(id+"F0.wireOp",EDGE,"E43.MirrorCS")])]})]});
            var Q34;
            Q34=makeQuery(id+"F2.opShell","TWEAK_EDGE",EDGE,{"derivedFrom":[makeQuery(id+"F1.opExtrude","SWEPT_FACE",FACE,{"disambiguationData":[OSD([sQuery(id+"F0.wireOp",EDGE,"E23.MirrorCS")])]}),makeQuery(id+"F1.opExtrude","SWEPT_FACE",FACE,{"disambiguationData":[OSD([sQuery(id+"F0.wireOp",EDGE,"E68.trimOffspring")])]})]});
            var Q35;
            Q35=makeQuery(id+"F2.opShell","TWEAK_EDGE",EDGE,{"derivedFrom":[makeQuery(id+"F1.opExtrude","SWEPT_FACE",FACE,{"disambiguationData":[OSD([sQuery(id+"F0.wireOp",EDGE,"E2.left")])]}),makeQuery(id+"F1.opExtrude","SWEPT_FACE",FACE,{"disambiguationData":[OSD([sQuery(id+"F0.wireOp",EDGE,"E14")])]})]});
            var Q36;
            Q36=makeQuery(id+"F2.opShell","TWEAK_EDGE",EDGE,{"derivedFrom":[makeQuery(id+"F1.opExtrude","SWEPT_FACE",FACE,{"disambiguationData":[OSD([sQuery(id+"F0.wireOp",EDGE,"E2.top")])]}),makeQuery(id+"F1.opExtrude","SWEPT_FACE",FACE,{"disambiguationData":[OSD([sQuery(id+"F0.wireOp",EDGE,"E56.MirrorCS")])]})]});
            var Q37;
            Q37=makeQuery(id+"F2.opShell","TWEAK_EDGE",EDGE,{"derivedFrom":[makeQuery(id+"F1.opExtrude","SWEPT_FACE",FACE,{"disambiguationData":[OSD([sQuery(id+"F0.wireOp",EDGE,"E2.top")])]}),makeQuery(id+"F1.opExtrude","SWEPT_FACE",FACE,{"disambiguationData":[OSD([sQuery(id+"F0.wireOp",EDGE,"E59.MirrorCS")])]})]});
            var Q38;
            Q38=makeQuery(id+"F2.opShell","TWEAK_EDGE",EDGE,{"derivedFrom":[makeQuery(id+"F1.opExtrude","SWEPT_FACE",FACE,{"disambiguationData":[OSD([sQuery(id+"F0.wireOp",EDGE,"E2.right")])]}),makeQuery(id+"F1.opExtrude","SWEPT_FACE",FACE,{"disambiguationData":[OSD([sQuery(id+"F0.wireOp",EDGE,"E28.MirrorCS")])]})]});
            var Q39;
            Q39=makeQuery(id+"F2.opShell","TWEAK_EDGE",EDGE,{"derivedFrom":[makeQuery(id+"F1.opExtrude","SWEPT_FACE",FACE,{"disambiguationData":[OSD([sQuery(id+"F0.wireOp",EDGE,"E2.right")])]}),makeQuery(id+"F1.opExtrude","SWEPT_FACE",FACE,{"disambiguationData":[OSD([sQuery(id+"F0.wireOp",EDGE,"E26.MirrorCS")])]})]});
            fillet(context, id + "F11", {"entities" : qUnion([Q0, Q1, Q2, Q3, Q4, Q5, Q6, Q7, Q8, Q9, Q10, Q11, Q12, Q13, Q14, Q15, Q16, Q17, Q18, Q19, Q20, Q21, Q22, Q23, Q24, Q25, Q26, Q27, Q28, Q29, Q30, Q31, Q32, Q33, Q34, Q35, Q36, Q37, Q38, Q39]), "radius" : 2 * mm, "tangentPropagation" : true, "allowEdgeOverflow" : false});
        }
        {
            var Q0;
            Q0=makeQuery(id+"F5.opExtrude","SWEPT_EDGE",EDGE,{"disambiguationData":[OSD([sQuery(id+"F4.wireOp",EDGE,"E84.MirrorCS"),sQuery(id+"F4.wireOp",EDGE,"E87.MirrorCS")])]});
            var Q1;
            Q1=makeQuery(id+"F5.opExtrude","SWEPT_EDGE",EDGE,{"disambiguationData":[OSD([sQuery(id+"F4.wireOp",EDGE,"E84.MirrorCS"),sQuery(id+"F4.wireOp",EDGE,"E88.MirrorCS")])]});
            var Q2;
            Q2=makeQuery(id+"F5.opExtrude","SWEPT_EDGE",EDGE,{"disambiguationData":[OSD([sQuery(id+"F4.wireOp",EDGE,"E122.MirrorCS"),sQuery(id+"F4.wireOp",EDGE,"E123.MirrorCS")])]});
            var Q3;
            Q3=makeQuery(id+"F5.opExtrude","SWEPT_EDGE",EDGE,{"disambiguationData":[OSD([sQuery(id+"F4.wireOp",EDGE,"E118.MirrorCS"),sQuery(id+"F4.wireOp",EDGE,"E122.MirrorCS")])]});
            var Q4;
            Q4=makeQuery(id+"F5.opExtrude","SWEPT_EDGE",EDGE,{"disambiguationData":[OSD([sQuery(id+"F4.wireOp",EDGE,"E113.MirrorCS"),sQuery(id+"F4.wireOp",EDGE,"E116.MirrorCS")])]});
            var Q5;
            Q5=makeQuery(id+"F5.opExtrude","SWEPT_EDGE",EDGE,{"disambiguationData":[OSD([sQuery(id+"F4.wireOp",EDGE,"E113.MirrorCS"),sQuery(id+"F4.wireOp",EDGE,"E115.MirrorCS")])]});
            var Q6;
            Q6=makeQuery(id+"F5.opExtrude","SWEPT_EDGE",EDGE,{"disambiguationData":[OSD([sQuery(id+"F4.wireOp",EDGE,"E76.top"),sQuery(id+"F4.wireOp",EDGE,"E76.right")])]});
            var Q7;
            Q7=makeQuery(id+"F5.opExtrude","SWEPT_EDGE",EDGE,{"disambiguationData":[OSD([sQuery(id+"F4.wireOp",EDGE,"E76.bottom"),sQuery(id+"F4.wireOp",EDGE,"E76.right")])]});
            var Q8;
            Q8=makeQuery(id+"F5.opExtrude","SWEPT_EDGE",EDGE,{"disambiguationData":[OSD([sQuery(id+"F4.wireOp",EDGE,"E96.MirrorCS"),sQuery(id+"F4.wireOp",EDGE,"E99.MirrorCS")])]});
            var Q9;
            Q9=makeQuery(id+"F5.opExtrude","SWEPT_EDGE",EDGE,{"disambiguationData":[OSD([sQuery(id+"F4.wireOp",EDGE,"E97.MirrorCS"),sQuery(id+"F4.wireOp",EDGE,"E99.MirrorCS")])]});
            var Q10;
            Q10=makeQuery(id+"F5.opExtrude","SWEPT_EDGE",EDGE,{"disambiguationData":[OSD([sQuery(id+"F4.wireOp",EDGE,"E127.MirrorCS"),sQuery(id+"F4.wireOp",EDGE,"E138.MirrorCS")])]});
            var Q11;
            Q11=makeQuery(id+"F5.opExtrude","SWEPT_EDGE",EDGE,{"disambiguationData":[OSD([sQuery(id+"F4.wireOp",EDGE,"E138.MirrorCS"),sQuery(id+"F4.wireOp",EDGE,"E140.MirrorCS")])]});
            var Q12;
            Q12=makeQuery(id+"F5.opExtrude","SWEPT_EDGE",EDGE,{"disambiguationData":[OSD([sQuery(id+"F4.wireOp",EDGE,"E134.MirrorCS"),sQuery(id+"F4.wireOp",EDGE,"E137.MirrorCS")])]});
            var Q13;
            Q13=makeQuery(id+"F5.opExtrude","SWEPT_EDGE",EDGE,{"disambiguationData":[OSD([sQuery(id+"F4.wireOp",EDGE,"E126.MirrorCS"),sQuery(id+"F4.wireOp",EDGE,"E137.MirrorCS")])]});
            var Q14;
            Q14=makeQuery(id+"F5.opExtrude","SWEPT_EDGE",EDGE,{"disambiguationData":[OSD([sQuery(id+"F4.wireOp",EDGE,"E95.MirrorCS"),sQuery(id+"F4.wireOp",EDGE,"E103.MirrorCS")])]});
            var Q15;
            Q15=makeQuery(id+"F5.opExtrude","SWEPT_EDGE",EDGE,{"disambiguationData":[OSD([sQuery(id+"F4.wireOp",EDGE,"E94.MirrorCS"),sQuery(id+"F4.wireOp",EDGE,"E103.MirrorCS")])]});
            fillet(context, id + "F12", {"entities" : qUnion([Q0, Q1, Q2, Q3, Q4, Q5, Q6, Q7, Q8, Q9, Q10, Q11, Q12, Q13, Q14, Q15]), "radius" : 1 * mm, "tangentPropagation" : true, "allowEdgeOverflow" : false});
        }
        {
            var Q0;
            Q0=makeQuery(id+"F5.opExtrude","SWEPT_EDGE",EDGE,{"disambiguationData":[OSD([sQuery(id+"F0.wireOp",EDGE,"E58.MirrorCS"),sQuery(id+"F4.wireOp",EDGE,"E114.MirrorCS"),sQuery(id+"F4.wireOp",EDGE,"E115.MirrorCS")])]});
            var Q1;
            Q1=makeQuery(id+"F5.opExtrude","SWEPT_EDGE",EDGE,{"disambiguationData":[OSD([sQuery(id+"F0.wireOp",EDGE,"E15"),sQuery(id+"F4.wireOp",EDGE,"E76.bottom"),sQuery(id+"F4.wireOp",EDGE,"E76.left")])]});
            var Q2;
            Q2=makeQuery(id+"F5.opExtrude","SWEPT_EDGE",EDGE,{"disambiguationData":[OSD([sQuery(id+"F0.wireOp",EDGE,"E23.MirrorCS"),sQuery(id+"F4.wireOp",EDGE,"E96.MirrorCS"),sQuery(id+"F4.wireOp",EDGE,"E98.MirrorCS")])]});
            var Q3;
            Q3=makeQuery(id+"F5.opExtrude","SWEPT_EDGE",EDGE,{"disambiguationData":[OSD([sQuery(id+"F0.wireOp",EDGE,"E40.MirrorCS"),sQuery(id+"F4.wireOp",EDGE,"E135.MirrorCS"),sQuery(id+"F4.wireOp",EDGE,"E140.MirrorCS")])]});
            var Q4;
            Q4=makeQuery(id+"F5.opExtrude","SWEPT_EDGE",EDGE,{"disambiguationData":[OSD([sQuery(id+"F0.wireOp",EDGE,"E52.MirrorCS"),sQuery(id+"F4.wireOp",EDGE,"E133.MirrorCS"),sQuery(id+"F4.wireOp",EDGE,"E134.MirrorCS")])]});
            var Q5;
            Q5=makeQuery(id+"F5.opExtrude","SWEPT_EDGE",EDGE,{"disambiguationData":[OSD([sQuery(id+"F0.wireOp",EDGE,"E35.MirrorCS"),sQuery(id+"F4.wireOp",EDGE,"E94.MirrorCS"),sQuery(id+"F4.wireOp",EDGE,"E107.MirrorCS")])]});
            var Q6;
            Q6=makeQuery(id+"F5.opExtrude","SWEPT_EDGE",EDGE,{"disambiguationData":[OSD([sQuery(id+"F0.wireOp",EDGE,"E25.MirrorCS"),sQuery(id+"F4.wireOp",EDGE,"E83.MirrorCS"),sQuery(id+"F4.wireOp",EDGE,"E87.MirrorCS")])]});
            var Q7;
            Q7=makeQuery(id+"F5.opExtrude","SWEPT_EDGE",EDGE,{"disambiguationData":[OSD([sQuery(id+"F0.wireOp",EDGE,"E64.MirrorCS"),sQuery(id+"F4.wireOp",EDGE,"E123.MirrorCS"),sQuery(id+"F4.wireOp",EDGE,"E124.MirrorCS")])]});
            var Q8;
            Q8=makeQuery(id+"F2.opShell","TWEAK_EDGE",EDGE,{"derivedFrom":[makeQuery(id+"F1.opExtrude","SWEPT_FACE",FACE,{"disambiguationData":[OSD([sQuery(id+"F0.wireOp",EDGE,"E15")])]}),makeQuery(id+"F1.opExtrude","SWEPT_FACE",FACE,{"disambiguationData":[OSD([sQuery(id+"F0.wireOp",EDGE,"E75.trimOffspring")])]})]});
            var Q9;
            Q9=makeQuery(id+"F2.opShell","TWEAK_EDGE",EDGE,{"derivedFrom":[makeQuery(id+"F1.opExtrude","SWEPT_FACE",FACE,{"disambiguationData":[OSD([sQuery(id+"F0.wireOp",EDGE,"E9.MirrorCS")])]}),makeQuery(id+"F1.opExtrude","SWEPT_FACE",FACE,{"disambiguationData":[OSD([sQuery(id+"F0.wireOp",EDGE,"E58.MirrorCS")])]})]});
            var Q10;
            Q10=makeQuery(id+"F2.opShell","TWEAK_EDGE",EDGE,{"derivedFrom":[makeQuery(id+"F1.opExtrude","SWEPT_FACE",FACE,{"disambiguationData":[OSD([sQuery(id+"F0.wireOp",EDGE,"E23.MirrorCS")])]}),makeQuery(id+"F1.opExtrude","SWEPT_FACE",FACE,{"disambiguationData":[OSD([sQuery(id+"F0.wireOp",EDGE,"E68.trimOffspring")])]})]});
            var Q11;
            Q11=makeQuery(id+"F2.opShell","TWEAK_EDGE",EDGE,{"derivedFrom":[makeQuery(id+"F1.opExtrude","SWEPT_FACE",FACE,{"disambiguationData":[OSD([sQuery(id+"F0.wireOp",EDGE,"E4")])]}),makeQuery(id+"F1.opExtrude","SWEPT_FACE",FACE,{"disambiguationData":[OSD([sQuery(id+"F0.wireOp",EDGE,"E40.MirrorCS")])]})]});
            var Q12;
            Q12=makeQuery(id+"F2.opShell","TWEAK_EDGE",EDGE,{"derivedFrom":[makeQuery(id+"F1.opExtrude","SWEPT_FACE",FACE,{"disambiguationData":[OSD([sQuery(id+"F0.wireOp",EDGE,"E6.MirrorCS")])]}),makeQuery(id+"F1.opExtrude","SWEPT_FACE",FACE,{"disambiguationData":[OSD([sQuery(id+"F0.wireOp",EDGE,"E52.MirrorCS")])]})]});
            var Q13;
            Q13=makeQuery(id+"F2.opShell","TWEAK_EDGE",EDGE,{"derivedFrom":[makeQuery(id+"F1.opExtrude","SWEPT_FACE",FACE,{"disambiguationData":[OSD([sQuery(id+"F0.wireOp",EDGE,"E35.MirrorCS")])]}),makeQuery(id+"F1.opExtrude","SWEPT_FACE",FACE,{"disambiguationData":[OSD([sQuery(id+"F0.wireOp",EDGE,"E71.trimOffspring")])]})]});
            var Q14;
            Q14=makeQuery(id+"F2.opShell","TWEAK_EDGE",EDGE,{"derivedFrom":[makeQuery(id+"F1.opExtrude","SWEPT_FACE",FACE,{"disambiguationData":[OSD([sQuery(id+"F0.wireOp",EDGE,"E25.MirrorCS")])]}),makeQuery(id+"F1.opExtrude","SWEPT_FACE",FACE,{"disambiguationData":[OSD([sQuery(id+"F0.wireOp",EDGE,"E72.trimOffspring")])]})]});
            var Q15;
            Q15=makeQuery(id+"F2.opShell","TWEAK_EDGE",EDGE,{"derivedFrom":[makeQuery(id+"F1.opExtrude","SWEPT_FACE",FACE,{"disambiguationData":[OSD([sQuery(id+"F0.wireOp",EDGE,"E7.MirrorCS")])]}),makeQuery(id+"F1.opExtrude","SWEPT_FACE",FACE,{"disambiguationData":[OSD([sQuery(id+"F0.wireOp",EDGE,"E64.MirrorCS")])]})]});
            fillet(context, id + "F13", {"entities" : qUnion([Q0, Q1, Q2, Q3, Q4, Q5, Q6, Q7, Q8, Q9, Q10, Q11, Q12, Q13, Q14, Q15]), "radius" : 2 * mm, "tangentPropagation" : true, "allowEdgeOverflow" : false});
        }
        {
            var Q0;
            Q0=makeQuery(id+"F5.opExtrude","SWEPT_EDGE",EDGE,{"disambiguationData":[OSD([sQuery(id+"F4.wireOp",EDGE,"E151.MirrorCS"),sQuery(id+"F4.wireOp",EDGE,"E149.MirrorCS")])]});
            var Q1;
            Q1=makeQuery(id+"F5.opExtrude","SWEPT_EDGE",EDGE,{"disambiguationData":[OSD([sQuery(id+"F4.wireOp",EDGE,"E152.MirrorCS"),sQuery(id+"F4.wireOp",EDGE,"E149.MirrorCS")])]});
            var Q2;
            Q2=makeQuery(id+"F5.opExtrude","SWEPT_EDGE",EDGE,{"disambiguationData":[OSD([sQuery(id+"F4.wireOp",EDGE,"E152.MirrorCS"),sQuery(id+"F4.wireOp",EDGE,"E150.MirrorCS")])]});
            var Q3;
            Q3=makeQuery(id+"F5.opExtrude","SWEPT_EDGE",EDGE,{"disambiguationData":[OSD([sQuery(id+"F4.wireOp",EDGE,"E151.MirrorCS"),sQuery(id+"F4.wireOp",EDGE,"E150.MirrorCS")])]});
            var Q4;
            Q4=makeQuery(id+"F5.opExtrude","SWEPT_EDGE",EDGE,{"disambiguationData":[OSD([sQuery(id+"F4.wireOp",EDGE,"E156.MirrorCS"),sQuery(id+"F4.wireOp",EDGE,"E161.MirrorCS")])]});
            var Q5;
            Q5=makeQuery(id+"F5.opExtrude","SWEPT_EDGE",EDGE,{"disambiguationData":[OSD([sQuery(id+"F4.wireOp",EDGE,"E156.MirrorCS"),sQuery(id+"F4.wireOp",EDGE,"E162.MirrorCS")])]});
            var Q6;
            Q6=makeQuery(id+"F5.opExtrude","SWEPT_EDGE",EDGE,{"disambiguationData":[OSD([sQuery(id+"F4.wireOp",EDGE,"E155.MirrorCS"),sQuery(id+"F4.wireOp",EDGE,"E161.MirrorCS")])]});
            var Q7;
            Q7=makeQuery(id+"F5.opExtrude","SWEPT_EDGE",EDGE,{"disambiguationData":[OSD([sQuery(id+"F4.wireOp",EDGE,"E155.MirrorCS"),sQuery(id+"F4.wireOp",EDGE,"E162.MirrorCS")])]});
            var Q8;
            Q8=makeQuery(id+"F5.opExtrude","SWEPT_EDGE",EDGE,{"disambiguationData":[OSD([sQuery(id+"F4.wireOp",EDGE,"E159.MirrorCS"),sQuery(id+"F4.wireOp",EDGE,"E163.MirrorCS")])]});
            var Q9;
            Q9=makeQuery(id+"F5.opExtrude","SWEPT_EDGE",EDGE,{"disambiguationData":[OSD([sQuery(id+"F4.wireOp",EDGE,"E160.MirrorCS"),sQuery(id+"F4.wireOp",EDGE,"E163.MirrorCS")])]});
            var Q10;
            Q10=makeQuery(id+"F5.opExtrude","SWEPT_EDGE",EDGE,{"disambiguationData":[OSD([sQuery(id+"F4.wireOp",EDGE,"E160.MirrorCS"),sQuery(id+"F4.wireOp",EDGE,"E164.MirrorCS")])]});
            var Q11;
            Q11=makeQuery(id+"F5.opExtrude","SWEPT_EDGE",EDGE,{"disambiguationData":[OSD([sQuery(id+"F4.wireOp",EDGE,"E159.MirrorCS"),sQuery(id+"F4.wireOp",EDGE,"E164.MirrorCS")])]});
            var Q12;
            Q12=makeQuery(id+"F5.opExtrude","SWEPT_EDGE",EDGE,{"disambiguationData":[OSD([sQuery(id+"F4.wireOp",EDGE,"E142.0"),sQuery(id+"F4.wireOp",EDGE,"E145")])]});
            var Q13;
            Q13=makeQuery(id+"F5.opExtrude","SWEPT_EDGE",EDGE,{"disambiguationData":[OSD([sQuery(id+"F4.wireOp",EDGE,"E141"),sQuery(id+"F4.wireOp",EDGE,"E145")])]});
            var Q14;
            Q14=makeQuery(id+"F5.opExtrude","SWEPT_EDGE",EDGE,{"disambiguationData":[OSD([sQuery(id+"F4.wireOp",EDGE,"E142.0"),sQuery(id+"F4.wireOp",EDGE,"E146")])]});
            var Q15;
            Q15=makeQuery(id+"F5.opExtrude","SWEPT_EDGE",EDGE,{"disambiguationData":[OSD([sQuery(id+"F4.wireOp",EDGE,"E141"),sQuery(id+"F4.wireOp",EDGE,"E146")])]});
            fillet(context, id + "F14", {"entities" : qUnion([Q0, Q1, Q2, Q3, Q4, Q5, Q6, Q7, Q8, Q9, Q10, Q11, Q12, Q13, Q14, Q15]), "radius" : 0.5 * mm, "tangentPropagation" : true, "allowEdgeOverflow" : false});
        }
        {
            var Q0;
            Q0=makeQuery(id+"F1.opExtrude","SWEPT_EDGE",EDGE,{"disambiguationData":[OSD([sQuery(id+"F0.wireOp",EDGE,"E17"),sQuery(id+"F0.wireOp",EDGE,"E75.trimOffspring")])]});
            var Q1;
            Q1=makeQuery(id+"F1.opExtrude","SWEPT_EDGE",EDGE,{"disambiguationData":[OSD([sQuery(id+"F0.wireOp",EDGE,"E16"),sQuery(id+"F0.wireOp",EDGE,"E17")])]});
            var Q2;
            Q2=makeQuery(id+"F1.opExtrude","SWEPT_EDGE",EDGE,{"disambiguationData":[OSD([sQuery(id+"F0.wireOp",EDGE,"E10.MirrorCS"),sQuery(id+"F0.wireOp",EDGE,"E11")])]});
            var Q3;
            Q3=makeQuery(id+"F1.opExtrude","SWEPT_EDGE",EDGE,{"disambiguationData":[OSD([sQuery(id+"F0.wireOp",EDGE,"E11"),sQuery(id+"F0.wireOp",EDGE,"E12")])]});
            var Q4;
            Q4=makeQuery(id+"F1.opExtrude","SWEPT_EDGE",EDGE,{"disambiguationData":[OSD([sQuery(id+"F0.wireOp",EDGE,"E61.MirrorCS"),sQuery(id+"F0.wireOp",EDGE,"E62.MirrorCS")])]});
            var Q5;
            Q5=makeQuery(id+"F1.opExtrude","SWEPT_EDGE",EDGE,{"disambiguationData":[OSD([sQuery(id+"F0.wireOp",EDGE,"E9.MirrorCS"),sQuery(id+"F0.wireOp",EDGE,"E61.MirrorCS")])]});
            var Q6;
            Q6=makeQuery(id+"F1.opExtrude","SWEPT_EDGE",EDGE,{"disambiguationData":[OSD([sQuery(id+"F0.wireOp",EDGE,"E57.MirrorCS"),sQuery(id+"F0.wireOp",EDGE,"E60.MirrorCS")])]});
            var Q7;
            Q7=makeQuery(id+"F1.opExtrude","SWEPT_EDGE",EDGE,{"disambiguationData":[OSD([sQuery(id+"F0.wireOp",EDGE,"E60.MirrorCS"),sQuery(id+"F0.wireOp",EDGE,"E74.trimOffspring")])]});
            var Q8;
            Q8=makeQuery(id+"F1.opExtrude","SWEPT_EDGE",EDGE,{"disambiguationData":[OSD([sQuery(id+"F0.wireOp",EDGE,"E55.MirrorCS"),sQuery(id+"F0.wireOp",EDGE,"E66.MirrorCS")])]});
            var Q9;
            Q9=makeQuery(id+"F1.opExtrude","SWEPT_EDGE",EDGE,{"disambiguationData":[OSD([sQuery(id+"F0.wireOp",EDGE,"E55.MirrorCS"),sQuery(id+"F0.wireOp",EDGE,"E73.trimOffspring")])]});
            var Q10;
            Q10=makeQuery(id+"F1.opExtrude","SWEPT_EDGE",EDGE,{"disambiguationData":[OSD([sQuery(id+"F0.wireOp",EDGE,"E63.MirrorCS"),sQuery(id+"F0.wireOp",EDGE,"E65.MirrorCS")])]});
            var Q11;
            Q11=makeQuery(id+"F1.opExtrude","SWEPT_EDGE",EDGE,{"disambiguationData":[OSD([sQuery(id+"F0.wireOp",EDGE,"E7.MirrorCS"),sQuery(id+"F0.wireOp",EDGE,"E63.MirrorCS")])]});
            var Q12;
            Q12=makeQuery(id+"F1.opExtrude","SWEPT_EDGE",EDGE,{"disambiguationData":[OSD([sQuery(id+"F0.wireOp",EDGE,"E8.MirrorCS"),sQuery(id+"F0.wireOp",EDGE,"E36.MirrorCS")])]});
            var Q13;
            Q13=makeQuery(id+"F1.opExtrude","SWEPT_EDGE",EDGE,{"disambiguationData":[OSD([sQuery(id+"F0.wireOp",EDGE,"E36.MirrorCS"),sQuery(id+"F0.wireOp",EDGE,"E38.MirrorCS")])]});
            var Q14;
            Q14=makeQuery(id+"F1.opExtrude","SWEPT_EDGE",EDGE,{"disambiguationData":[OSD([sQuery(id+"F0.wireOp",EDGE,"E32.MirrorCS"),sQuery(id+"F0.wireOp",EDGE,"E72.trimOffspring")])]});
            var Q15;
            Q15=makeQuery(id+"F1.opExtrude","SWEPT_EDGE",EDGE,{"disambiguationData":[OSD([sQuery(id+"F0.wireOp",EDGE,"E32.MirrorCS"),sQuery(id+"F0.wireOp",EDGE,"E37.MirrorCS")])]});
            var Q16;
            Q16=makeQuery(id+"F1.opExtrude","SWEPT_EDGE",EDGE,{"disambiguationData":[OSD([sQuery(id+"F0.wireOp",EDGE,"E29.MirrorCS"),sQuery(id+"F0.wireOp",EDGE,"E34.MirrorCS")])]});
            var Q17;
            Q17=makeQuery(id+"F1.opExtrude","SWEPT_EDGE",EDGE,{"disambiguationData":[OSD([sQuery(id+"F0.wireOp",EDGE,"E34.MirrorCS"),sQuery(id+"F0.wireOp",EDGE,"E71.trimOffspring")])]});
            var Q18;
            Q18=makeQuery(id+"F1.opExtrude","SWEPT_EDGE",EDGE,{"disambiguationData":[OSD([sQuery(id+"F0.wireOp",EDGE,"E27.MirrorCS"),sQuery(id+"F0.wireOp",EDGE,"E33.MirrorCS")])]});
            var Q19;
            Q19=makeQuery(id+"F1.opExtrude","SWEPT_EDGE",EDGE,{"disambiguationData":[OSD([sQuery(id+"F0.wireOp",EDGE,"E5.MirrorCS"),sQuery(id+"F0.wireOp",EDGE,"E33.MirrorCS")])]});
            var Q20;
            Q20=makeQuery(id+"F1.opExtrude","SWEPT_EDGE",EDGE,{"disambiguationData":[OSD([sQuery(id+"F0.wireOp",EDGE,"E47.MirrorCS"),sQuery(id+"F0.wireOp",EDGE,"E50.MirrorCS")])]});
            var Q21;
            Q21=makeQuery(id+"F1.opExtrude","SWEPT_EDGE",EDGE,{"disambiguationData":[OSD([sQuery(id+"F0.wireOp",EDGE,"E50.MirrorCS"),sQuery(id+"F0.wireOp",EDGE,"E70.trimOffspring")])]});
            var Q22;
            Q22=makeQuery(id+"F1.opExtrude","SWEPT_EDGE",EDGE,{"disambiguationData":[OSD([sQuery(id+"F0.wireOp",EDGE,"E49.MirrorCS"),sQuery(id+"F0.wireOp",EDGE,"E53.MirrorCS")])]});
            var Q23;
            Q23=makeQuery(id+"F1.opExtrude","SWEPT_EDGE",EDGE,{"disambiguationData":[OSD([sQuery(id+"F0.wireOp",EDGE,"E6.MirrorCS"),sQuery(id+"F0.wireOp",EDGE,"E53.MirrorCS")])]});
            var Q24;
            Q24=makeQuery(id+"F1.opExtrude","SWEPT_EDGE",EDGE,{"disambiguationData":[OSD([sQuery(id+"F0.wireOp",EDGE,"E45.MirrorCS"),sQuery(id+"F0.wireOp",EDGE,"E46.MirrorCS")])]});
            var Q25;
            Q25=makeQuery(id+"F1.opExtrude","SWEPT_EDGE",EDGE,{"disambiguationData":[OSD([sQuery(id+"F0.wireOp",EDGE,"E45.MirrorCS"),sQuery(id+"F0.wireOp",EDGE,"E69.trimOffspring")])]});
            var Q26;
            Q26=makeQuery(id+"F1.opExtrude","SWEPT_EDGE",EDGE,{"disambiguationData":[OSD([sQuery(id+"F0.wireOp",EDGE,"E4"),sQuery(id+"F0.wireOp",EDGE,"E42.MirrorCS")])]});
            var Q27;
            Q27=makeQuery(id+"F1.opExtrude","SWEPT_EDGE",EDGE,{"disambiguationData":[OSD([sQuery(id+"F0.wireOp",EDGE,"E41.MirrorCS"),sQuery(id+"F0.wireOp",EDGE,"E42.MirrorCS")])]});
            var Q28;
            Q28=makeQuery(id+"F1.opExtrude","SWEPT_EDGE",EDGE,{"disambiguationData":[OSD([sQuery(id+"F0.wireOp",EDGE,"E18.MirrorCS"),sQuery(id+"F0.wireOp",EDGE,"E24.MirrorCS")])]});
            var Q29;
            Q29=makeQuery(id+"F1.opExtrude","SWEPT_EDGE",EDGE,{"disambiguationData":[OSD([sQuery(id+"F0.wireOp",EDGE,"E24.MirrorCS"),sQuery(id+"F0.wireOp",EDGE,"E68.trimOffspring")])]});
            var Q30;
            Q30=makeQuery(id+"F1.opExtrude","SWEPT_EDGE",EDGE,{"disambiguationData":[OSD([sQuery(id+"F0.wireOp",EDGE,"E20.MirrorCS"),sQuery(id+"F0.wireOp",EDGE,"E22.MirrorCS")])]});
            var Q31;
            Q31=makeQuery(id+"F1.opExtrude","SWEPT_EDGE",EDGE,{"disambiguationData":[OSD([sQuery(id+"F0.wireOp",EDGE,"E3"),sQuery(id+"F0.wireOp",EDGE,"E20.MirrorCS")])]});
            fillet(context, id + "F15", {"entities" : qUnion([Q0, Q1, Q2, Q3, Q4, Q5, Q6, Q7, Q8, Q9, Q10, Q11, Q12, Q13, Q14, Q15, Q16, Q17, Q18, Q19, Q20, Q21, Q22, Q23, Q24, Q25, Q26, Q27, Q28, Q29, Q30, Q31]), "radius" : 0.5 * mm, "tangentPropagation" : true, "allowEdgeOverflow" : false});
        }
    });
